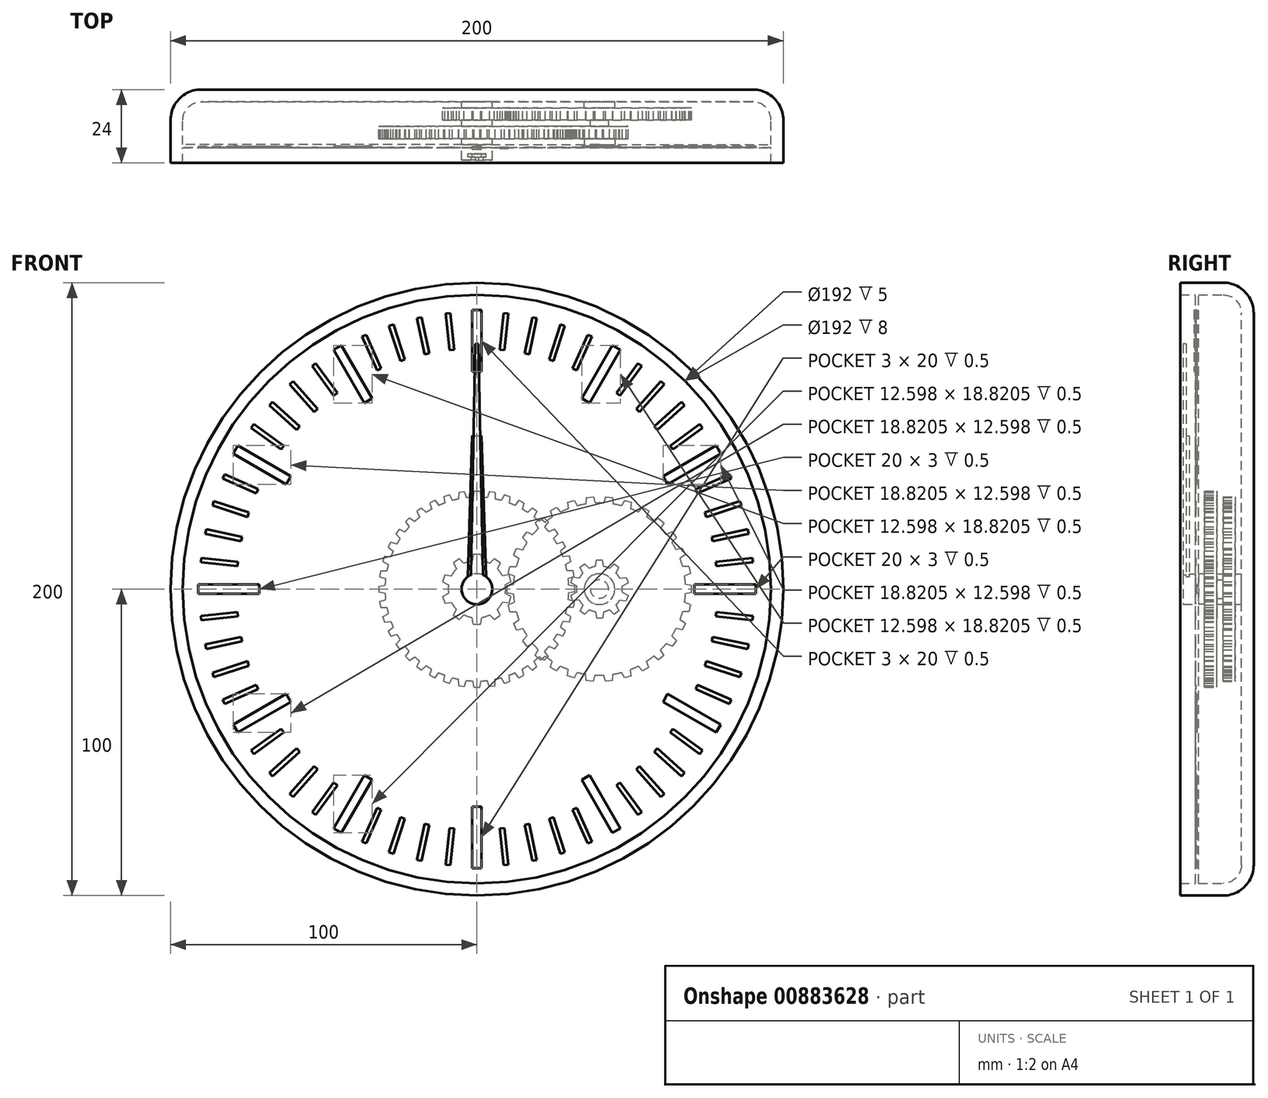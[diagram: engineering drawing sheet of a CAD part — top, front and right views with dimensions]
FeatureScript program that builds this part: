
annotation { "Feature Type Name" : "Feature", "Feature Type Description" : "" }
export const myFeature = defineFeature(function(context is Context, id is Id, definition is map)
    precondition{}
    {
        {
            var Q0;
            Q0=qCreatedBy(makeId("Front.planeOp"),FACE);
            var sketch = newSketch(context, id + "F0", { "sketchPlane" : qUnion([Q0])});
            skCircle(sketch, "E0", {"center": v(0, 0) * mm, "radius": 100 * mm});
            skSolve(sketch);
        }
        {
            var Q0;
            Q0 = qSketchRegion(id + "F0", true);
            extrude(context, id + "F1", {"entities" : qUnion([Q0]), "depth" : 24 * mm, "offsetDistance" : 25 * mm});
        }
        {
            var Q0;
            Q0=makeQuery(id+"F1.opExtrude","CAP_EDGE",EDGE,{"disambiguationData":[OSD([sQuery(id+"F0.wireOp",EDGE,"E0")])],"isStart":true});
            fillet(context, id + "F2", {"entities" : qUnion([Q0]), "radius" : 10 * mm, "tangentPropagation" : true, "allowEdgeOverflow" : false});
        }
        {
            var Q0;
            Q0=makeQuery(id+"F1.opExtrude","CAP_FACE",FACE,{"disambiguationData":[OSD([sQuery(id+"F0.wireOp",EDGE,"E0")])],"isStart":false});
            shell(context, id + "F3", {"entities" : qUnion([Q0]), "thickness" : 4 * mm});
        }
        {
            var Q0;
            {var subQ0=sQuery(id+"F0.wireOp",EDGE,"E0");Q0=makeQuery(id+"F3.opShell","OFFSET_FACE",FACE,{"disambiguationData":[OSD([subQ0]),TDD([makeQuery(id+"F1.opExtrude","CAP_FACE",FACE,{"disambiguationData":[OSD([subQ0])],"isStart":true})])]});}
            var sketch = newSketch(context, id + "F4", { "sketchPlane" : qUnion([Q0])});
            skCircle(sketch, "E1", {"center": v(0, 0) * mm, "radius": 3 * mm});
            skCircle(sketch, "E2", {"center": v(0, 0) * mm, "radius": 5 * mm});
            skCircle(sketch, "E3", {"center": v(40, 0) * mm, "radius": 3 * mm});
            skCircle(sketch, "E4", {"center": v(40, 0) * mm, "radius": 5 * mm});
            skSolve(sketch);
        }
        {
            var Q0;
            Q0 = qSketchRegion(id + "F4", true);
            extrude(context, id + "F5", {"entities" : qUnion([Q0]), "operationType" : NewBodyOperationType.ADD, "depth" : 2 * mm, "offsetDistance" : 25 * mm});
        }
        {
            var Q0;
            {var subQ0=sQuery(id+"F0.wireOp",EDGE,"E0");Q0=makeQuery(id+"F5.boolean.opBoolean","SPLIT",FACE,{"disambiguationData":[TD([makeQuery(id+"F5.opExtrude","SWEPT_FACE",FACE,{"disambiguationData":[OSD([sQuery(id+"F4.wireOp",EDGE,"E1")])]})])],"derivedFrom":makeQuery(id+"F3.opShell","OFFSET_FACE",FACE,{"disambiguationData":[OSD([subQ0]),TDD([makeQuery(id+"F1.opExtrude","CAP_FACE",FACE,{"disambiguationData":[OSD([subQ0])],"isStart":true})])]})});}
            extrude(context, id + "F6", {"entities" : qUnion([Q0]), "depth" : 19 * mm, "offsetDistance" : 25 * mm});
        }
        {
            var Q0;
            {var subQ0=sQuery(id+"F0.wireOp",EDGE,"E0");Q0=makeQuery(id+"F5.boolean.opBoolean","SPLIT",FACE,{"disambiguationData":[TD([makeQuery(id+"F5.opExtrude","SWEPT_FACE",FACE,{"disambiguationData":[OSD([sQuery(id+"F4.wireOp",EDGE,"E3")])]})])],"derivedFrom":makeQuery(id+"F3.opShell","OFFSET_FACE",FACE,{"disambiguationData":[OSD([subQ0]),TDD([makeQuery(id+"F1.opExtrude","CAP_FACE",FACE,{"disambiguationData":[OSD([subQ0])],"isStart":true})])]})});}
            extrude(context, id + "F7", {"entities" : qUnion([Q0]), "depth" : 8 * mm, "offsetDistance" : 25 * mm});
        }
        {
            var Q0;
            Q0=makeQuery(id+"F5.opExtrude","CAP_FACE",FACE,{"disambiguationData":[OSD([sQuery(id+"F4.wireOp",EDGE,"E1"),sQuery(id+"F4.wireOp",EDGE,"E2")])],"isStart":false});
            var sketch = newSketch(context, id + "F8", { "sketchPlane" : qUnion([Q0])});
            skCircle(sketch, "E5", {"center": v(0, 0) * mm, "radius": 9.38 * mm});
            skLineSegment(sketch, "E6", {"start": v(0, 11.38) * mm, "end": v(1.18, 11.38) * mm});
            skLineSegment(sketch, "E7", {"start": v(1.18, 11.38) * mm, "end": v(1.55, 9.25) * mm});
            skLineSegment(sketch, "E8.MirrorCS", {"start": v(0, 11.38) * mm, "end": v(-1.18, 11.38) * mm});
            skLineSegment(sketch, "E9.MirrorCS", {"start": v(-1.18, 11.38) * mm, "end": v(-1.55, 9.25) * mm});
            skLineSegment(sketch, "E10.1.0", {"start": v(-7.64, 8.51) * mm, "end": v(-6.7, 6.57) * mm});
            skLineSegment(sketch, "E10.1.1", {"start": v(-6.69, 9.2) * mm, "end": v(-7.64, 8.51) * mm});
            skLineSegment(sketch, "E10.1.2", {"start": v(-6.69, 9.2) * mm, "end": v(-5.73, 9.9) * mm});
            skLineSegment(sketch, "E10.1.3", {"start": v(-5.73, 9.9) * mm, "end": v(-4.18, 8.4) * mm});
            skLineSegment(sketch, "E10.2.0", {"start": v(-11.18, 2.4) * mm, "end": v(-9.27, 1.38) * mm});
            skLineSegment(sketch, "E10.2.1", {"start": v(-10.82, 3.52) * mm, "end": v(-11.18, 2.4) * mm});
            skLineSegment(sketch, "E10.2.2", {"start": v(-10.82, 3.52) * mm, "end": v(-10.45, 4.64) * mm});
            skLineSegment(sketch, "E10.2.3", {"start": v(-10.45, 4.64) * mm, "end": v(-8.31, 4.33) * mm});
            skLineSegment(sketch, "E11.2.3.0", {"start": v(-10.45, -4.64) * mm, "end": v(-8.31, -4.33) * mm});
            skLineSegment(sketch, "E11.3.3.0", {"start": v(-10.82, -3.52) * mm, "end": v(-10.45, -4.64) * mm});
            skLineSegment(sketch, "E11.6.3.0", {"start": v(-10.82, -3.52) * mm, "end": v(-11.18, -2.4) * mm});
            skLineSegment(sketch, "E11.9.3.0", {"start": v(-11.18, -2.4) * mm, "end": v(-9.27, -1.38) * mm});
            skLineSegment(sketch, "E11.2.4.0", {"start": v(-5.73, -9.9) * mm, "end": v(-4.18, -8.4) * mm});
            skLineSegment(sketch, "E11.3.4.0", {"start": v(-6.69, -9.2) * mm, "end": v(-5.73, -9.9) * mm});
            skLineSegment(sketch, "E11.6.4.0", {"start": v(-6.69, -9.2) * mm, "end": v(-7.64, -8.51) * mm});
            skLineSegment(sketch, "E11.9.4.0", {"start": v(-7.64, -8.51) * mm, "end": v(-6.7, -6.57) * mm});
            skLineSegment(sketch, "E11.2.5.0", {"start": v(1.18, -11.38) * mm, "end": v(1.55, -9.25) * mm});
            skLineSegment(sketch, "E11.3.5.0", {"start": v(0, -11.38) * mm, "end": v(1.18, -11.38) * mm});
            skLineSegment(sketch, "E11.6.5.0", {"start": v(0, -11.38) * mm, "end": v(-1.18, -11.38) * mm});
            skLineSegment(sketch, "E11.9.5.0", {"start": v(-1.18, -11.38) * mm, "end": v(-1.55, -9.25) * mm});
            skLineSegment(sketch, "E11.2.6.0", {"start": v(7.64, -8.51) * mm, "end": v(6.7, -6.57) * mm});
            skLineSegment(sketch, "E11.3.6.0", {"start": v(6.69, -9.2) * mm, "end": v(7.64, -8.51) * mm});
            skLineSegment(sketch, "E11.6.6.0", {"start": v(6.69, -9.2) * mm, "end": v(5.73, -9.9) * mm});
            skLineSegment(sketch, "E11.9.6.0", {"start": v(5.73, -9.9) * mm, "end": v(4.18, -8.4) * mm});
            skLineSegment(sketch, "E11.2.7.0", {"start": v(11.18, -2.4) * mm, "end": v(9.27, -1.38) * mm});
            skLineSegment(sketch, "E11.3.7.0", {"start": v(10.82, -3.52) * mm, "end": v(11.18, -2.4) * mm});
            skLineSegment(sketch, "E11.6.7.0", {"start": v(10.82, -3.52) * mm, "end": v(10.45, -4.64) * mm});
            skLineSegment(sketch, "E11.9.7.0", {"start": v(10.45, -4.64) * mm, "end": v(8.31, -4.33) * mm});
            skLineSegment(sketch, "E11.2.8.0", {"start": v(10.45, 4.64) * mm, "end": v(8.31, 4.33) * mm});
            skLineSegment(sketch, "E11.3.8.0", {"start": v(10.82, 3.52) * mm, "end": v(10.45, 4.64) * mm});
            skLineSegment(sketch, "E11.6.8.0", {"start": v(10.82, 3.52) * mm, "end": v(11.18, 2.4) * mm});
            skLineSegment(sketch, "E11.9.8.0", {"start": v(11.18, 2.4) * mm, "end": v(9.27, 1.38) * mm});
            skLineSegment(sketch, "E11.2.9.0", {"start": v(5.73, 9.9) * mm, "end": v(4.18, 8.4) * mm});
            skLineSegment(sketch, "E11.3.9.0", {"start": v(6.69, 9.2) * mm, "end": v(5.73, 9.9) * mm});
            skLineSegment(sketch, "E11.6.9.0", {"start": v(6.69, 9.2) * mm, "end": v(7.64, 8.51) * mm});
            skLineSegment(sketch, "E11.9.9.0", {"start": v(7.64, 8.51) * mm, "end": v(6.7, 6.57) * mm});
            skSolve(sketch);
        }
        {
            var Q0;
            Q0 = qSketchRegion(id + "F8", true);
            extrude(context, id + "F9", {"entities" : qUnion([Q0]), "operationType" : NewBodyOperationType.ADD, "depth" : 4 * mm, "offsetDistance" : 25 * mm});
        }
        {
            var Q0;
            Q0=makeQuery(id+"F5.opExtrude","CAP_FACE",FACE,{"disambiguationData":[OSD([sQuery(id+"F4.wireOp",EDGE,"E3"),sQuery(id+"F4.wireOp",EDGE,"E4")])],"isStart":false});
            var sketch = newSketch(context, id + "F10", { "sketchPlane" : qUnion([Q0])});
            skCircle(sketch, "E12", {"center": v(40, 0) * mm, "radius": 28.12 * mm});
            skLineSegment(sketch, "E13", {"start": v(9.88, 0) * mm, "end": v(9.88, 1.18) * mm});
            skLineSegment(sketch, "E14", {"start": v(9.88, 1.18) * mm, "end": v(11.92, 1.54) * mm});
            skLineSegment(sketch, "E15.MirrorCS", {"start": v(9.88, 0) * mm, "end": v(9.88, -1.18) * mm});
            skLineSegment(sketch, "E16.MirrorCS", {"start": v(9.88, -1.18) * mm, "end": v(11.92, -1.54) * mm});
            skLineSegment(sketch, "E17.1.0", {"start": v(10.29, -5.11) * mm, "end": v(12.21, -4.33) * mm});
            skLineSegment(sketch, "E17.1.1", {"start": v(10.53, -6.26) * mm, "end": v(10.29, -5.11) * mm});
            skLineSegment(sketch, "E17.1.2", {"start": v(10.53, -6.26) * mm, "end": v(10.78, -7.42) * mm});
            skLineSegment(sketch, "E17.1.3", {"start": v(10.78, -7.42) * mm, "end": v(12.85, -7.34) * mm});
            skLineSegment(sketch, "E17.2.0", {"start": v(12, -11.18) * mm, "end": v(13.72, -10.02) * mm});
            skLineSegment(sketch, "E17.2.1", {"start": v(12.48, -12.25) * mm, "end": v(12, -11.18) * mm});
            skLineSegment(sketch, "E17.2.2", {"start": v(12.48, -12.25) * mm, "end": v(12.96, -13.33) * mm});
            skLineSegment(sketch, "E17.2.3", {"start": v(12.96, -13.33) * mm, "end": v(14.97, -12.83) * mm});
            skLineSegment(sketch, "E18.1.3.0", {"start": v(14.94, -16.75) * mm, "end": v(16.38, -15.26) * mm});
            skLineSegment(sketch, "E18.3.3.0", {"start": v(15.63, -17.7) * mm, "end": v(14.94, -16.75) * mm});
            skLineSegment(sketch, "E18.6.3.0", {"start": v(15.63, -17.7) * mm, "end": v(16.32, -18.66) * mm});
            skLineSegment(sketch, "E18.9.3.0", {"start": v(16.32, -18.66) * mm, "end": v(18.18, -17.75) * mm});
            skLineSegment(sketch, "E18.1.4.0", {"start": v(18.97, -21.6) * mm, "end": v(20.07, -19.84) * mm});
            skLineSegment(sketch, "E18.3.4.0", {"start": v(19.84, -22.39) * mm, "end": v(18.97, -21.6) * mm});
            skLineSegment(sketch, "E18.6.4.0", {"start": v(19.84, -22.39) * mm, "end": v(20.72, -23.18) * mm});
            skLineSegment(sketch, "E18.9.4.0", {"start": v(20.72, -23.18) * mm, "end": v(22.35, -21.9) * mm});
            skLineSegment(sketch, "E18.1.5.0", {"start": v(23.92, -25.5) * mm, "end": v(24.63, -23.55) * mm});
            skLineSegment(sketch, "E18.3.5.0", {"start": v(24.94, -26.09) * mm, "end": v(23.92, -25.5) * mm});
            skLineSegment(sketch, "E18.6.5.0", {"start": v(24.94, -26.09) * mm, "end": v(25.96, -26.68) * mm});
            skLineSegment(sketch, "E18.9.5.0", {"start": v(25.96, -26.68) * mm, "end": v(27.3, -25.09) * mm});
            skLineSegment(sketch, "E18.1.6.0", {"start": v(29.57, -28.29) * mm, "end": v(29.86, -26.23) * mm});
            skLineSegment(sketch, "E18.3.6.0", {"start": v(30.7, -28.65) * mm, "end": v(29.57, -28.29) * mm});
            skLineSegment(sketch, "E18.6.6.0", {"start": v(30.7, -28.65) * mm, "end": v(31.81, -29.01) * mm});
            skLineSegment(sketch, "E18.9.6.0", {"start": v(31.81, -29.01) * mm, "end": v(32.78, -27.18) * mm});
            skLineSegment(sketch, "E18.1.7.0", {"start": v(35.68, -29.84) * mm, "end": v(35.53, -27.77) * mm});
            skLineSegment(sketch, "E18.3.7.0", {"start": v(36.85, -29.96) * mm, "end": v(35.68, -29.84) * mm});
            skLineSegment(sketch, "E18.6.7.0", {"start": v(36.85, -29.96) * mm, "end": v(38.02, -30.08) * mm});
            skLineSegment(sketch, "E18.9.7.0", {"start": v(38.02, -30.08) * mm, "end": v(38.6, -28.09) * mm});
            skLineSegment(sketch, "E18.1.8.0", {"start": v(41.98, -30.08) * mm, "end": v(41.4, -28.09) * mm});
            skLineSegment(sketch, "E18.3.8.0", {"start": v(43.15, -29.96) * mm, "end": v(41.98, -30.08) * mm});
            skLineSegment(sketch, "E18.6.8.0", {"start": v(43.15, -29.96) * mm, "end": v(44.32, -29.84) * mm});
            skLineSegment(sketch, "E18.9.8.0", {"start": v(44.32, -29.84) * mm, "end": v(44.47, -27.77) * mm});
            skLineSegment(sketch, "E18.1.9.0", {"start": v(48.19, -29.01) * mm, "end": v(47.22, -27.18) * mm});
            skLineSegment(sketch, "E18.3.9.0", {"start": v(49.3, -28.65) * mm, "end": v(48.19, -29.01) * mm});
            skLineSegment(sketch, "E18.6.9.0", {"start": v(49.3, -28.65) * mm, "end": v(50.43, -28.29) * mm});
            skLineSegment(sketch, "E18.9.9.0", {"start": v(50.43, -28.29) * mm, "end": v(50.14, -26.23) * mm});
            skLineSegment(sketch, "E18.1.10.0", {"start": v(54.04, -26.68) * mm, "end": v(52.7, -25.09) * mm});
            skLineSegment(sketch, "E18.3.10.0", {"start": v(55.06, -26.09) * mm, "end": v(54.04, -26.68) * mm});
            skLineSegment(sketch, "E18.6.10.0", {"start": v(55.06, -26.09) * mm, "end": v(56.08, -25.5) * mm});
            skLineSegment(sketch, "E18.9.10.0", {"start": v(56.08, -25.5) * mm, "end": v(55.37, -23.55) * mm});
            skLineSegment(sketch, "E18.1.11.0", {"start": v(59.28, -23.18) * mm, "end": v(57.65, -21.9) * mm});
            skLineSegment(sketch, "E18.3.11.0", {"start": v(60.16, -22.39) * mm, "end": v(59.28, -23.18) * mm});
            skLineSegment(sketch, "E18.6.11.0", {"start": v(60.16, -22.39) * mm, "end": v(61.03, -21.6) * mm});
            skLineSegment(sketch, "E18.9.11.0", {"start": v(61.03, -21.6) * mm, "end": v(59.93, -19.84) * mm});
            skLineSegment(sketch, "E18.1.12.0", {"start": v(63.68, -18.66) * mm, "end": v(61.82, -17.75) * mm});
            skLineSegment(sketch, "E18.3.12.0", {"start": v(64.37, -17.7) * mm, "end": v(63.68, -18.66) * mm});
            skLineSegment(sketch, "E18.6.12.0", {"start": v(64.37, -17.7) * mm, "end": v(65.06, -16.75) * mm});
            skLineSegment(sketch, "E18.9.12.0", {"start": v(65.06, -16.75) * mm, "end": v(63.62, -15.26) * mm});
            skLineSegment(sketch, "E18.1.13.0", {"start": v(67.04, -13.33) * mm, "end": v(65.03, -12.83) * mm});
            skLineSegment(sketch, "E18.3.13.0", {"start": v(67.52, -12.25) * mm, "end": v(67.04, -13.33) * mm});
            skLineSegment(sketch, "E18.6.13.0", {"start": v(67.52, -12.25) * mm, "end": v(68, -11.18) * mm});
            skLineSegment(sketch, "E18.9.13.0", {"start": v(68, -11.18) * mm, "end": v(66.28, -10.02) * mm});
            skLineSegment(sketch, "E18.1.14.0", {"start": v(69.22, -7.42) * mm, "end": v(67.15, -7.34) * mm});
            skLineSegment(sketch, "E18.3.14.0", {"start": v(69.47, -6.26) * mm, "end": v(69.22, -7.42) * mm});
            skLineSegment(sketch, "E18.6.14.0", {"start": v(69.47, -6.26) * mm, "end": v(69.71, -5.11) * mm});
            skLineSegment(sketch, "E18.9.14.0", {"start": v(69.71, -5.11) * mm, "end": v(67.79, -4.33) * mm});
            skLineSegment(sketch, "E18.1.15.0", {"start": v(70.12, -1.18) * mm, "end": v(68.08, -1.54) * mm});
            skLineSegment(sketch, "E18.3.15.0", {"start": v(70.12, 0) * mm, "end": v(70.12, -1.18) * mm});
            skLineSegment(sketch, "E18.6.15.0", {"start": v(70.12, 0) * mm, "end": v(70.12, 1.18) * mm});
            skLineSegment(sketch, "E18.9.15.0", {"start": v(70.12, 1.18) * mm, "end": v(68.08, 1.54) * mm});
            skLineSegment(sketch, "E18.1.16.0", {"start": v(69.71, 5.11) * mm, "end": v(67.79, 4.33) * mm});
            skLineSegment(sketch, "E18.3.16.0", {"start": v(69.47, 6.26) * mm, "end": v(69.71, 5.11) * mm});
            skLineSegment(sketch, "E18.6.16.0", {"start": v(69.47, 6.26) * mm, "end": v(69.22, 7.42) * mm});
            skLineSegment(sketch, "E18.9.16.0", {"start": v(69.22, 7.42) * mm, "end": v(67.15, 7.34) * mm});
            skLineSegment(sketch, "E18.1.17.0", {"start": v(68, 11.18) * mm, "end": v(66.28, 10.02) * mm});
            skLineSegment(sketch, "E18.3.17.0", {"start": v(67.52, 12.25) * mm, "end": v(68, 11.18) * mm});
            skLineSegment(sketch, "E18.6.17.0", {"start": v(67.52, 12.25) * mm, "end": v(67.04, 13.33) * mm});
            skLineSegment(sketch, "E18.9.17.0", {"start": v(67.04, 13.33) * mm, "end": v(65.03, 12.83) * mm});
            skLineSegment(sketch, "E18.1.18.0", {"start": v(65.06, 16.75) * mm, "end": v(63.62, 15.26) * mm});
            skLineSegment(sketch, "E18.3.18.0", {"start": v(64.37, 17.7) * mm, "end": v(65.06, 16.75) * mm});
            skLineSegment(sketch, "E18.6.18.0", {"start": v(64.37, 17.7) * mm, "end": v(63.68, 18.66) * mm});
            skLineSegment(sketch, "E18.9.18.0", {"start": v(63.68, 18.66) * mm, "end": v(61.82, 17.75) * mm});
            skLineSegment(sketch, "E18.1.19.0", {"start": v(61.03, 21.6) * mm, "end": v(59.93, 19.84) * mm});
            skLineSegment(sketch, "E18.3.19.0", {"start": v(60.16, 22.39) * mm, "end": v(61.03, 21.6) * mm});
            skLineSegment(sketch, "E18.6.19.0", {"start": v(60.16, 22.39) * mm, "end": v(59.28, 23.18) * mm});
            skLineSegment(sketch, "E18.9.19.0", {"start": v(59.28, 23.18) * mm, "end": v(57.65, 21.9) * mm});
            skLineSegment(sketch, "E18.1.20.0", {"start": v(56.08, 25.5) * mm, "end": v(55.37, 23.55) * mm});
            skLineSegment(sketch, "E18.3.20.0", {"start": v(55.06, 26.09) * mm, "end": v(56.08, 25.5) * mm});
            skLineSegment(sketch, "E18.6.20.0", {"start": v(55.06, 26.09) * mm, "end": v(54.04, 26.68) * mm});
            skLineSegment(sketch, "E18.9.20.0", {"start": v(54.04, 26.68) * mm, "end": v(52.7, 25.09) * mm});
            skLineSegment(sketch, "E18.1.21.0", {"start": v(50.43, 28.29) * mm, "end": v(50.14, 26.23) * mm});
            skLineSegment(sketch, "E18.3.21.0", {"start": v(49.3, 28.65) * mm, "end": v(50.43, 28.29) * mm});
            skLineSegment(sketch, "E18.6.21.0", {"start": v(49.3, 28.65) * mm, "end": v(48.19, 29.01) * mm});
            skLineSegment(sketch, "E18.9.21.0", {"start": v(48.19, 29.01) * mm, "end": v(47.22, 27.18) * mm});
            skLineSegment(sketch, "E18.1.22.0", {"start": v(44.32, 29.84) * mm, "end": v(44.47, 27.77) * mm});
            skLineSegment(sketch, "E18.3.22.0", {"start": v(43.15, 29.96) * mm, "end": v(44.32, 29.84) * mm});
            skLineSegment(sketch, "E18.6.22.0", {"start": v(43.15, 29.96) * mm, "end": v(41.98, 30.08) * mm});
            skLineSegment(sketch, "E18.9.22.0", {"start": v(41.98, 30.08) * mm, "end": v(41.4, 28.09) * mm});
            skLineSegment(sketch, "E18.1.23.0", {"start": v(38.02, 30.08) * mm, "end": v(38.6, 28.09) * mm});
            skLineSegment(sketch, "E18.3.23.0", {"start": v(36.85, 29.96) * mm, "end": v(38.02, 30.08) * mm});
            skLineSegment(sketch, "E18.6.23.0", {"start": v(36.85, 29.96) * mm, "end": v(35.68, 29.84) * mm});
            skLineSegment(sketch, "E18.9.23.0", {"start": v(35.68, 29.84) * mm, "end": v(35.53, 27.77) * mm});
            skLineSegment(sketch, "E18.1.24.0", {"start": v(31.81, 29.01) * mm, "end": v(32.78, 27.18) * mm});
            skLineSegment(sketch, "E18.3.24.0", {"start": v(30.7, 28.65) * mm, "end": v(31.81, 29.01) * mm});
            skLineSegment(sketch, "E18.6.24.0", {"start": v(30.7, 28.65) * mm, "end": v(29.57, 28.29) * mm});
            skLineSegment(sketch, "E18.9.24.0", {"start": v(29.57, 28.29) * mm, "end": v(29.86, 26.23) * mm});
            skLineSegment(sketch, "E18.1.25.0", {"start": v(25.96, 26.68) * mm, "end": v(27.3, 25.09) * mm});
            skLineSegment(sketch, "E18.3.25.0", {"start": v(24.94, 26.09) * mm, "end": v(25.96, 26.68) * mm});
            skLineSegment(sketch, "E18.6.25.0", {"start": v(24.94, 26.09) * mm, "end": v(23.92, 25.5) * mm});
            skLineSegment(sketch, "E18.9.25.0", {"start": v(23.92, 25.5) * mm, "end": v(24.63, 23.55) * mm});
            skLineSegment(sketch, "E18.1.26.0", {"start": v(20.72, 23.18) * mm, "end": v(22.35, 21.9) * mm});
            skLineSegment(sketch, "E18.3.26.0", {"start": v(19.84, 22.39) * mm, "end": v(20.72, 23.18) * mm});
            skLineSegment(sketch, "E18.6.26.0", {"start": v(19.84, 22.39) * mm, "end": v(18.97, 21.6) * mm});
            skLineSegment(sketch, "E18.9.26.0", {"start": v(18.97, 21.6) * mm, "end": v(20.07, 19.84) * mm});
            skLineSegment(sketch, "E18.1.27.0", {"start": v(16.32, 18.66) * mm, "end": v(18.18, 17.75) * mm});
            skLineSegment(sketch, "E18.3.27.0", {"start": v(15.63, 17.7) * mm, "end": v(16.32, 18.66) * mm});
            skLineSegment(sketch, "E18.6.27.0", {"start": v(15.63, 17.7) * mm, "end": v(14.94, 16.75) * mm});
            skLineSegment(sketch, "E18.9.27.0", {"start": v(14.94, 16.75) * mm, "end": v(16.38, 15.26) * mm});
            skLineSegment(sketch, "E18.1.28.0", {"start": v(12.96, 13.33) * mm, "end": v(14.97, 12.83) * mm});
            skLineSegment(sketch, "E18.3.28.0", {"start": v(12.48, 12.25) * mm, "end": v(12.96, 13.33) * mm});
            skLineSegment(sketch, "E18.6.28.0", {"start": v(12.48, 12.25) * mm, "end": v(12, 11.18) * mm});
            skLineSegment(sketch, "E18.9.28.0", {"start": v(12, 11.18) * mm, "end": v(13.72, 10.02) * mm});
            skLineSegment(sketch, "E18.1.29.0", {"start": v(10.78, 7.42) * mm, "end": v(12.85, 7.34) * mm});
            skLineSegment(sketch, "E18.3.29.0", {"start": v(10.53, 6.26) * mm, "end": v(10.78, 7.42) * mm});
            skLineSegment(sketch, "E18.6.29.0", {"start": v(10.53, 6.26) * mm, "end": v(10.29, 5.11) * mm});
            skLineSegment(sketch, "E18.9.29.0", {"start": v(10.29, 5.11) * mm, "end": v(12.21, 4.33) * mm});
            skSolve(sketch);
        }
        {
            var Q0;
            Q0 = qSketchRegion(id + "F10", true);
            extrude(context, id + "F11", {"entities" : qUnion([Q0]), "operationType" : NewBodyOperationType.ADD, "depth" : 4 * mm, "offsetDistance" : 25 * mm});
        }
        {
            var Q0;
            Q0=makeQuery(id+"F9.opExtrude","CAP_FACE",FACE,{"disambiguationData":[OSD([sQuery(id+"F8.wireOp",EDGE,"E5"),sQuery(id+"F8.wireOp",EDGE,"E6"),sQuery(id+"F8.wireOp",EDGE,"E7"),sQuery(id+"F8.wireOp",EDGE,"E8.MirrorCS"),sQuery(id+"F8.wireOp",EDGE,"E9.MirrorCS"),sQuery(id+"F8.wireOp",EDGE,"E10.1.0"),sQuery(id+"F8.wireOp",EDGE,"E10.1.1"),sQuery(id+"F8.wireOp",EDGE,"E10.1.2"),sQuery(id+"F8.wireOp",EDGE,"E10.1.3"),sQuery(id+"F8.wireOp",EDGE,"E10.2.0"),sQuery(id+"F8.wireOp",EDGE,"E10.2.1"),sQuery(id+"F8.wireOp",EDGE,"E10.2.2"),sQuery(id+"F8.wireOp",EDGE,"E10.2.3"),sQuery(id+"F8.wireOp",EDGE,"E11.2.3.0"),sQuery(id+"F8.wireOp",EDGE,"E11.3.3.0"),sQuery(id+"F8.wireOp",EDGE,"E11.6.3.0"),sQuery(id+"F8.wireOp",EDGE,"E11.9.3.0"),sQuery(id+"F8.wireOp",EDGE,"E11.2.4.0"),sQuery(id+"F8.wireOp",EDGE,"E11.3.4.0"),sQuery(id+"F8.wireOp",EDGE,"E11.6.4.0"),sQuery(id+"F8.wireOp",EDGE,"E11.9.4.0"),sQuery(id+"F8.wireOp",EDGE,"E11.2.5.0"),sQuery(id+"F8.wireOp",EDGE,"E11.3.5.0"),sQuery(id+"F8.wireOp",EDGE,"E11.6.5.0"),sQuery(id+"F8.wireOp",EDGE,"E11.9.5.0"),sQuery(id+"F8.wireOp",EDGE,"E11.2.6.0"),sQuery(id+"F8.wireOp",EDGE,"E11.3.6.0"),sQuery(id+"F8.wireOp",EDGE,"E11.6.6.0"),sQuery(id+"F8.wireOp",EDGE,"E11.9.6.0"),sQuery(id+"F8.wireOp",EDGE,"E11.2.7.0"),sQuery(id+"F8.wireOp",EDGE,"E11.3.7.0"),sQuery(id+"F8.wireOp",EDGE,"E11.6.7.0"),sQuery(id+"F8.wireOp",EDGE,"E11.9.7.0"),sQuery(id+"F8.wireOp",EDGE,"E11.2.8.0"),sQuery(id+"F8.wireOp",EDGE,"E11.3.8.0"),sQuery(id+"F8.wireOp",EDGE,"E11.6.8.0"),sQuery(id+"F8.wireOp",EDGE,"E11.9.8.0"),sQuery(id+"F8.wireOp",EDGE,"E11.2.9.0"),sQuery(id+"F8.wireOp",EDGE,"E11.3.9.0"),sQuery(id+"F8.wireOp",EDGE,"E11.6.9.0"),sQuery(id+"F8.wireOp",EDGE,"E11.9.9.0")])],"isStart":false});
            var sketch = newSketch(context, id + "F12", { "sketchPlane" : qUnion([Q0])});
            skCircle(sketch, "E19.0", {"center": v(0, 0) * mm, "radius": 5 * mm});
            skCircle(sketch, "E20.0", {"center": v(0, 0) * mm, "radius": 3 * mm});
            skSolve(sketch);
        }
        {
            var Q0;
            Q0 = qSketchRegion(id + "F12", true);
            extrude(context, id + "F13", {"entities" : qUnion([Q0]), "depth" : 2 * mm, "offsetDistance" : 25 * mm});
        }
        {
            var Q0;
            Q0=makeQuery(id+"F13.opExtrude","CAP_FACE",FACE,{"disambiguationData":[OSD([sQuery(id+"F12.wireOp",EDGE,"E19.0"),sQuery(id+"F12.wireOp",EDGE,"E20.0")])],"isStart":false});
            var sketch = newSketch(context, id + "F14", { "sketchPlane" : qUnion([Q0])});
            skCircle(sketch, "E21.0", {"center": v(0, 0) * mm, "radius": 3 * mm});
            skCircle(sketch, "E22", {"center": v(0, 0) * mm, "radius": 30 * mm});
            skLineSegment(sketch, "E23", {"start": v(0, 32) * mm, "end": v(0.94, 32) * mm});
            skLineSegment(sketch, "E24", {"start": v(0.94, 32) * mm, "end": v(1.3, 29.97) * mm});
            skLineSegment(sketch, "E25.MirrorCS", {"start": v(0, 32) * mm, "end": v(-0.94, 32) * mm});
            skLineSegment(sketch, "E26.MirrorCS", {"start": v(-0.94, 32) * mm, "end": v(-1.3, 29.97) * mm});
            skLineSegment(sketch, "E27.1.0", {"start": v(-5.94, 31.46) * mm, "end": v(-5.97, 29.4) * mm});
            skLineSegment(sketch, "E27.1.1", {"start": v(-5, 31.6) * mm, "end": v(-5.94, 31.46) * mm});
            skLineSegment(sketch, "E27.1.2", {"start": v(-5, 31.6) * mm, "end": v(-4.08, 31.75) * mm});
            skLineSegment(sketch, "E27.1.3", {"start": v(-4.08, 31.75) * mm, "end": v(-3.4, 29.8) * mm});
            skLineSegment(sketch, "E27.2.0", {"start": v(-10.78, 30.14) * mm, "end": v(-10.5, 28.1) * mm});
            skLineSegment(sketch, "E27.2.1", {"start": v(-9.89, 30.43) * mm, "end": v(-10.78, 30.14) * mm});
            skLineSegment(sketch, "E27.2.2", {"start": v(-9.89, 30.43) * mm, "end": v(-9, 30.73) * mm});
            skLineSegment(sketch, "E27.2.3", {"start": v(-9, 30.73) * mm, "end": v(-8.03, 28.9) * mm});
            skLineSegment(sketch, "E28.2.3.0", {"start": v(-15.37, 28.08) * mm, "end": v(-14.77, 26.11) * mm});
            skLineSegment(sketch, "E28.3.3.0", {"start": v(-14.53, 28.51) * mm, "end": v(-15.37, 28.08) * mm});
            skLineSegment(sketch, "E28.6.3.0", {"start": v(-14.53, 28.51) * mm, "end": v(-13.69, 28.94) * mm});
            skLineSegment(sketch, "E28.9.3.0", {"start": v(-13.69, 28.94) * mm, "end": v(-12.45, 27.3) * mm});
            skLineSegment(sketch, "E28.2.4.0", {"start": v(-19.57, 25.33) * mm, "end": v(-18.67, 23.48) * mm});
            skLineSegment(sketch, "E28.3.4.0", {"start": v(-18.8, 25.89) * mm, "end": v(-19.57, 25.33) * mm});
            skLineSegment(sketch, "E28.6.4.0", {"start": v(-18.8, 25.89) * mm, "end": v(-18.05, 26.44) * mm});
            skLineSegment(sketch, "E28.9.4.0", {"start": v(-18.05, 26.44) * mm, "end": v(-16.57, 25.01) * mm});
            skLineSegment(sketch, "E28.2.5.0", {"start": v(-23.3, 21.96) * mm, "end": v(-22.11, 20.27) * mm});
            skLineSegment(sketch, "E28.3.5.0", {"start": v(-22.63, 22.63) * mm, "end": v(-23.3, 21.96) * mm});
            skLineSegment(sketch, "E28.6.5.0", {"start": v(-22.63, 22.63) * mm, "end": v(-21.96, 23.3) * mm});
            skLineSegment(sketch, "E28.9.5.0", {"start": v(-21.96, 23.3) * mm, "end": v(-20.27, 22.11) * mm});
            skLineSegment(sketch, "E28.2.6.0", {"start": v(-26.44, 18.05) * mm, "end": v(-25.01, 16.57) * mm});
            skLineSegment(sketch, "E28.3.6.0", {"start": v(-25.89, 18.8) * mm, "end": v(-26.44, 18.05) * mm});
            skLineSegment(sketch, "E28.6.6.0", {"start": v(-25.89, 18.8) * mm, "end": v(-25.33, 19.57) * mm});
            skLineSegment(sketch, "E28.9.6.0", {"start": v(-25.33, 19.57) * mm, "end": v(-23.48, 18.67) * mm});
            skLineSegment(sketch, "E28.2.7.0", {"start": v(-28.94, 13.69) * mm, "end": v(-27.3, 12.45) * mm});
            skLineSegment(sketch, "E28.3.7.0", {"start": v(-28.51, 14.53) * mm, "end": v(-28.94, 13.69) * mm});
            skLineSegment(sketch, "E28.6.7.0", {"start": v(-28.51, 14.53) * mm, "end": v(-28.08, 15.37) * mm});
            skLineSegment(sketch, "E28.9.7.0", {"start": v(-28.08, 15.37) * mm, "end": v(-26.11, 14.77) * mm});
            skLineSegment(sketch, "E28.2.8.0", {"start": v(-30.73, 9) * mm, "end": v(-28.9, 8.03) * mm});
            skLineSegment(sketch, "E28.3.8.0", {"start": v(-30.43, 9.89) * mm, "end": v(-30.73, 9) * mm});
            skLineSegment(sketch, "E28.6.8.0", {"start": v(-30.43, 9.89) * mm, "end": v(-30.14, 10.78) * mm});
            skLineSegment(sketch, "E28.9.8.0", {"start": v(-30.14, 10.78) * mm, "end": v(-28.1, 10.5) * mm});
            skLineSegment(sketch, "E28.2.9.0", {"start": v(-31.75, 4.08) * mm, "end": v(-29.8, 3.4) * mm});
            skLineSegment(sketch, "E28.3.9.0", {"start": v(-31.6, 5) * mm, "end": v(-31.75, 4.08) * mm});
            skLineSegment(sketch, "E28.6.9.0", {"start": v(-31.6, 5) * mm, "end": v(-31.46, 5.94) * mm});
            skLineSegment(sketch, "E28.9.9.0", {"start": v(-31.46, 5.94) * mm, "end": v(-29.4, 5.97) * mm});
            skLineSegment(sketch, "E28.2.10.0", {"start": v(-32, -0.94) * mm, "end": v(-29.97, -1.3) * mm});
            skLineSegment(sketch, "E28.3.10.0", {"start": v(-32, 0) * mm, "end": v(-32, -0.94) * mm});
            skLineSegment(sketch, "E28.6.10.0", {"start": v(-32, 0) * mm, "end": v(-32, 0.94) * mm});
            skLineSegment(sketch, "E28.9.10.0", {"start": v(-32, 0.94) * mm, "end": v(-29.97, 1.3) * mm});
            skLineSegment(sketch, "E28.2.11.0", {"start": v(-31.46, -5.94) * mm, "end": v(-29.4, -5.97) * mm});
            skLineSegment(sketch, "E28.3.11.0", {"start": v(-31.6, -5) * mm, "end": v(-31.46, -5.94) * mm});
            skLineSegment(sketch, "E28.6.11.0", {"start": v(-31.6, -5) * mm, "end": v(-31.75, -4.08) * mm});
            skLineSegment(sketch, "E28.9.11.0", {"start": v(-31.75, -4.08) * mm, "end": v(-29.8, -3.4) * mm});
            skLineSegment(sketch, "E28.2.12.0", {"start": v(-30.14, -10.78) * mm, "end": v(-28.1, -10.5) * mm});
            skLineSegment(sketch, "E28.3.12.0", {"start": v(-30.43, -9.89) * mm, "end": v(-30.14, -10.78) * mm});
            skLineSegment(sketch, "E28.6.12.0", {"start": v(-30.43, -9.89) * mm, "end": v(-30.73, -9) * mm});
            skLineSegment(sketch, "E28.9.12.0", {"start": v(-30.73, -9) * mm, "end": v(-28.9, -8.03) * mm});
            skLineSegment(sketch, "E28.2.13.0", {"start": v(-28.08, -15.37) * mm, "end": v(-26.11, -14.77) * mm});
            skLineSegment(sketch, "E28.3.13.0", {"start": v(-28.51, -14.53) * mm, "end": v(-28.08, -15.37) * mm});
            skLineSegment(sketch, "E28.6.13.0", {"start": v(-28.51, -14.53) * mm, "end": v(-28.94, -13.69) * mm});
            skLineSegment(sketch, "E28.9.13.0", {"start": v(-28.94, -13.69) * mm, "end": v(-27.3, -12.45) * mm});
            skLineSegment(sketch, "E28.2.14.0", {"start": v(-25.33, -19.57) * mm, "end": v(-23.48, -18.67) * mm});
            skLineSegment(sketch, "E28.3.14.0", {"start": v(-25.89, -18.8) * mm, "end": v(-25.33, -19.57) * mm});
            skLineSegment(sketch, "E28.6.14.0", {"start": v(-25.89, -18.8) * mm, "end": v(-26.44, -18.05) * mm});
            skLineSegment(sketch, "E28.9.14.0", {"start": v(-26.44, -18.05) * mm, "end": v(-25.01, -16.57) * mm});
            skLineSegment(sketch, "E28.2.15.0", {"start": v(-21.96, -23.3) * mm, "end": v(-20.27, -22.11) * mm});
            skLineSegment(sketch, "E28.3.15.0", {"start": v(-22.63, -22.63) * mm, "end": v(-21.96, -23.3) * mm});
            skLineSegment(sketch, "E28.6.15.0", {"start": v(-22.63, -22.63) * mm, "end": v(-23.3, -21.96) * mm});
            skLineSegment(sketch, "E28.9.15.0", {"start": v(-23.3, -21.96) * mm, "end": v(-22.11, -20.27) * mm});
            skLineSegment(sketch, "E28.2.16.0", {"start": v(-18.05, -26.44) * mm, "end": v(-16.57, -25.01) * mm});
            skLineSegment(sketch, "E28.3.16.0", {"start": v(-18.8, -25.89) * mm, "end": v(-18.05, -26.44) * mm});
            skLineSegment(sketch, "E28.6.16.0", {"start": v(-18.8, -25.89) * mm, "end": v(-19.57, -25.33) * mm});
            skLineSegment(sketch, "E28.9.16.0", {"start": v(-19.57, -25.33) * mm, "end": v(-18.67, -23.48) * mm});
            skLineSegment(sketch, "E28.2.17.0", {"start": v(-13.69, -28.94) * mm, "end": v(-12.45, -27.3) * mm});
            skLineSegment(sketch, "E28.3.17.0", {"start": v(-14.53, -28.51) * mm, "end": v(-13.69, -28.94) * mm});
            skLineSegment(sketch, "E28.6.17.0", {"start": v(-14.53, -28.51) * mm, "end": v(-15.37, -28.08) * mm});
            skLineSegment(sketch, "E28.9.17.0", {"start": v(-15.37, -28.08) * mm, "end": v(-14.77, -26.11) * mm});
            skLineSegment(sketch, "E28.2.18.0", {"start": v(-9, -30.73) * mm, "end": v(-8.03, -28.9) * mm});
            skLineSegment(sketch, "E28.3.18.0", {"start": v(-9.89, -30.43) * mm, "end": v(-9, -30.73) * mm});
            skLineSegment(sketch, "E28.6.18.0", {"start": v(-9.89, -30.43) * mm, "end": v(-10.78, -30.14) * mm});
            skLineSegment(sketch, "E28.9.18.0", {"start": v(-10.78, -30.14) * mm, "end": v(-10.5, -28.1) * mm});
            skLineSegment(sketch, "E28.2.19.0", {"start": v(-4.08, -31.75) * mm, "end": v(-3.4, -29.8) * mm});
            skLineSegment(sketch, "E28.3.19.0", {"start": v(-5, -31.6) * mm, "end": v(-4.08, -31.75) * mm});
            skLineSegment(sketch, "E28.6.19.0", {"start": v(-5, -31.6) * mm, "end": v(-5.94, -31.46) * mm});
            skLineSegment(sketch, "E28.9.19.0", {"start": v(-5.94, -31.46) * mm, "end": v(-5.97, -29.4) * mm});
            skLineSegment(sketch, "E28.2.20.0", {"start": v(0.94, -32) * mm, "end": v(1.3, -29.97) * mm});
            skLineSegment(sketch, "E28.3.20.0", {"start": v(0, -32) * mm, "end": v(0.94, -32) * mm});
            skLineSegment(sketch, "E28.6.20.0", {"start": v(0, -32) * mm, "end": v(-0.94, -32) * mm});
            skLineSegment(sketch, "E28.9.20.0", {"start": v(-0.94, -32) * mm, "end": v(-1.3, -29.97) * mm});
            skLineSegment(sketch, "E28.2.21.0", {"start": v(5.94, -31.46) * mm, "end": v(5.97, -29.4) * mm});
            skLineSegment(sketch, "E28.3.21.0", {"start": v(5, -31.6) * mm, "end": v(5.94, -31.46) * mm});
            skLineSegment(sketch, "E28.6.21.0", {"start": v(5, -31.6) * mm, "end": v(4.08, -31.75) * mm});
            skLineSegment(sketch, "E28.9.21.0", {"start": v(4.08, -31.75) * mm, "end": v(3.4, -29.8) * mm});
            skLineSegment(sketch, "E28.2.22.0", {"start": v(10.78, -30.14) * mm, "end": v(10.5, -28.1) * mm});
            skLineSegment(sketch, "E28.3.22.0", {"start": v(9.89, -30.43) * mm, "end": v(10.78, -30.14) * mm});
            skLineSegment(sketch, "E28.6.22.0", {"start": v(9.89, -30.43) * mm, "end": v(9, -30.73) * mm});
            skLineSegment(sketch, "E28.9.22.0", {"start": v(9, -30.73) * mm, "end": v(8.03, -28.9) * mm});
            skLineSegment(sketch, "E28.2.23.0", {"start": v(15.37, -28.08) * mm, "end": v(14.77, -26.11) * mm});
            skLineSegment(sketch, "E28.3.23.0", {"start": v(14.53, -28.51) * mm, "end": v(15.37, -28.08) * mm});
            skLineSegment(sketch, "E28.6.23.0", {"start": v(14.53, -28.51) * mm, "end": v(13.69, -28.94) * mm});
            skLineSegment(sketch, "E28.9.23.0", {"start": v(13.69, -28.94) * mm, "end": v(12.45, -27.3) * mm});
            skLineSegment(sketch, "E28.2.24.0", {"start": v(19.57, -25.33) * mm, "end": v(18.67, -23.48) * mm});
            skLineSegment(sketch, "E28.3.24.0", {"start": v(18.8, -25.89) * mm, "end": v(19.57, -25.33) * mm});
            skLineSegment(sketch, "E28.6.24.0", {"start": v(18.8, -25.89) * mm, "end": v(18.05, -26.44) * mm});
            skLineSegment(sketch, "E28.9.24.0", {"start": v(18.05, -26.44) * mm, "end": v(16.57, -25.01) * mm});
            skLineSegment(sketch, "E28.2.25.0", {"start": v(23.3, -21.96) * mm, "end": v(22.11, -20.27) * mm});
            skLineSegment(sketch, "E28.3.25.0", {"start": v(22.63, -22.63) * mm, "end": v(23.3, -21.96) * mm});
            skLineSegment(sketch, "E28.6.25.0", {"start": v(22.63, -22.63) * mm, "end": v(21.96, -23.3) * mm});
            skLineSegment(sketch, "E28.9.25.0", {"start": v(21.96, -23.3) * mm, "end": v(20.27, -22.11) * mm});
            skLineSegment(sketch, "E28.2.26.0", {"start": v(26.44, -18.05) * mm, "end": v(25.01, -16.57) * mm});
            skLineSegment(sketch, "E28.3.26.0", {"start": v(25.89, -18.8) * mm, "end": v(26.44, -18.05) * mm});
            skLineSegment(sketch, "E28.6.26.0", {"start": v(25.89, -18.8) * mm, "end": v(25.33, -19.57) * mm});
            skLineSegment(sketch, "E28.9.26.0", {"start": v(25.33, -19.57) * mm, "end": v(23.48, -18.67) * mm});
            skLineSegment(sketch, "E28.2.27.0", {"start": v(28.94, -13.69) * mm, "end": v(27.3, -12.45) * mm});
            skLineSegment(sketch, "E28.3.27.0", {"start": v(28.51, -14.53) * mm, "end": v(28.94, -13.69) * mm});
            skLineSegment(sketch, "E28.6.27.0", {"start": v(28.51, -14.53) * mm, "end": v(28.08, -15.37) * mm});
            skLineSegment(sketch, "E28.9.27.0", {"start": v(28.08, -15.37) * mm, "end": v(26.11, -14.77) * mm});
            skLineSegment(sketch, "E28.2.28.0", {"start": v(30.73, -9) * mm, "end": v(28.9, -8.03) * mm});
            skLineSegment(sketch, "E28.3.28.0", {"start": v(30.43, -9.89) * mm, "end": v(30.73, -9) * mm});
            skLineSegment(sketch, "E28.6.28.0", {"start": v(30.43, -9.89) * mm, "end": v(30.14, -10.78) * mm});
            skLineSegment(sketch, "E28.9.28.0", {"start": v(30.14, -10.78) * mm, "end": v(28.1, -10.5) * mm});
            skLineSegment(sketch, "E28.2.29.0", {"start": v(31.75, -4.08) * mm, "end": v(29.8, -3.4) * mm});
            skLineSegment(sketch, "E28.3.29.0", {"start": v(31.6, -5) * mm, "end": v(31.75, -4.08) * mm});
            skLineSegment(sketch, "E28.6.29.0", {"start": v(31.6, -5) * mm, "end": v(31.46, -5.94) * mm});
            skLineSegment(sketch, "E28.9.29.0", {"start": v(31.46, -5.94) * mm, "end": v(29.4, -5.97) * mm});
            skLineSegment(sketch, "E28.2.30.0", {"start": v(32, 0.94) * mm, "end": v(29.97, 1.3) * mm});
            skLineSegment(sketch, "E28.3.30.0", {"start": v(32, 0) * mm, "end": v(32, 0.94) * mm});
            skLineSegment(sketch, "E28.6.30.0", {"start": v(32, 0) * mm, "end": v(32, -0.94) * mm});
            skLineSegment(sketch, "E28.9.30.0", {"start": v(32, -0.94) * mm, "end": v(29.97, -1.3) * mm});
            skLineSegment(sketch, "E28.2.31.0", {"start": v(31.46, 5.94) * mm, "end": v(29.4, 5.97) * mm});
            skLineSegment(sketch, "E28.3.31.0", {"start": v(31.6, 5) * mm, "end": v(31.46, 5.94) * mm});
            skLineSegment(sketch, "E28.6.31.0", {"start": v(31.6, 5) * mm, "end": v(31.75, 4.08) * mm});
            skLineSegment(sketch, "E28.9.31.0", {"start": v(31.75, 4.08) * mm, "end": v(29.8, 3.4) * mm});
            skLineSegment(sketch, "E28.2.32.0", {"start": v(30.14, 10.78) * mm, "end": v(28.1, 10.5) * mm});
            skLineSegment(sketch, "E28.3.32.0", {"start": v(30.43, 9.89) * mm, "end": v(30.14, 10.78) * mm});
            skLineSegment(sketch, "E28.6.32.0", {"start": v(30.43, 9.89) * mm, "end": v(30.73, 9) * mm});
            skLineSegment(sketch, "E28.9.32.0", {"start": v(30.73, 9) * mm, "end": v(28.9, 8.03) * mm});
            skLineSegment(sketch, "E28.2.33.0", {"start": v(28.08, 15.37) * mm, "end": v(26.11, 14.77) * mm});
            skLineSegment(sketch, "E28.3.33.0", {"start": v(28.51, 14.53) * mm, "end": v(28.08, 15.37) * mm});
            skLineSegment(sketch, "E28.6.33.0", {"start": v(28.51, 14.53) * mm, "end": v(28.94, 13.69) * mm});
            skLineSegment(sketch, "E28.9.33.0", {"start": v(28.94, 13.69) * mm, "end": v(27.3, 12.45) * mm});
            skLineSegment(sketch, "E28.2.34.0", {"start": v(25.33, 19.57) * mm, "end": v(23.48, 18.67) * mm});
            skLineSegment(sketch, "E28.3.34.0", {"start": v(25.89, 18.8) * mm, "end": v(25.33, 19.57) * mm});
            skLineSegment(sketch, "E28.6.34.0", {"start": v(25.89, 18.8) * mm, "end": v(26.44, 18.05) * mm});
            skLineSegment(sketch, "E28.9.34.0", {"start": v(26.44, 18.05) * mm, "end": v(25.01, 16.57) * mm});
            skLineSegment(sketch, "E28.2.35.0", {"start": v(21.96, 23.3) * mm, "end": v(20.27, 22.11) * mm});
            skLineSegment(sketch, "E28.3.35.0", {"start": v(22.63, 22.63) * mm, "end": v(21.96, 23.3) * mm});
            skLineSegment(sketch, "E28.6.35.0", {"start": v(22.63, 22.63) * mm, "end": v(23.3, 21.96) * mm});
            skLineSegment(sketch, "E28.9.35.0", {"start": v(23.3, 21.96) * mm, "end": v(22.11, 20.27) * mm});
            skLineSegment(sketch, "E28.2.36.0", {"start": v(18.05, 26.44) * mm, "end": v(16.57, 25.01) * mm});
            skLineSegment(sketch, "E28.3.36.0", {"start": v(18.8, 25.89) * mm, "end": v(18.05, 26.44) * mm});
            skLineSegment(sketch, "E28.6.36.0", {"start": v(18.8, 25.89) * mm, "end": v(19.57, 25.33) * mm});
            skLineSegment(sketch, "E28.9.36.0", {"start": v(19.57, 25.33) * mm, "end": v(18.67, 23.48) * mm});
            skLineSegment(sketch, "E28.2.37.0", {"start": v(13.69, 28.94) * mm, "end": v(12.45, 27.3) * mm});
            skLineSegment(sketch, "E28.3.37.0", {"start": v(14.53, 28.51) * mm, "end": v(13.69, 28.94) * mm});
            skLineSegment(sketch, "E28.6.37.0", {"start": v(14.53, 28.51) * mm, "end": v(15.37, 28.08) * mm});
            skLineSegment(sketch, "E28.9.37.0", {"start": v(15.37, 28.08) * mm, "end": v(14.77, 26.11) * mm});
            skLineSegment(sketch, "E28.2.38.0", {"start": v(9, 30.73) * mm, "end": v(8.03, 28.9) * mm});
            skLineSegment(sketch, "E28.3.38.0", {"start": v(9.89, 30.43) * mm, "end": v(9, 30.73) * mm});
            skLineSegment(sketch, "E28.6.38.0", {"start": v(9.89, 30.43) * mm, "end": v(10.78, 30.14) * mm});
            skLineSegment(sketch, "E28.9.38.0", {"start": v(10.78, 30.14) * mm, "end": v(10.5, 28.1) * mm});
            skLineSegment(sketch, "E28.2.39.0", {"start": v(4.08, 31.75) * mm, "end": v(3.4, 29.8) * mm});
            skLineSegment(sketch, "E28.3.39.0", {"start": v(5, 31.6) * mm, "end": v(4.08, 31.75) * mm});
            skLineSegment(sketch, "E28.6.39.0", {"start": v(5, 31.6) * mm, "end": v(5.94, 31.46) * mm});
            skLineSegment(sketch, "E28.9.39.0", {"start": v(5.94, 31.46) * mm, "end": v(5.97, 29.4) * mm});
            skSolve(sketch);
        }
        {
            var Q0;
            Q0 = qSketchRegion(id + "F14", true);
            extrude(context, id + "F15", {"entities" : qUnion([Q0]), "operationType" : NewBodyOperationType.ADD, "depth" : 4 * mm, "offsetDistance" : 25 * mm});
        }
        {
            var Q0;
            Q0=makeQuery(id+"F7.opExtrude","CAP_FACE",FACE,{"disambiguationData":[OSD([sQuery(id+"F0.wireOp",EDGE,"E0")])],"isStart":false});
            var sketch = newSketch(context, id + "F16", { "sketchPlane" : qUnion([Q0])});
            skCircle(sketch, "E29", {"center": v(40, 0) * mm, "radius": 7.5 * mm});
            skLineSegment(sketch, "E30", {"start": v(40, 0) * mm, "end": v(40, 7.5) * mm, "construction": true});
            skLineSegment(sketch, "E31", {"start": v(38.68, 7.38) * mm, "end": v(39.06, 9.5) * mm});
            skLineSegment(sketch, "E32", {"start": v(39.06, 9.5) * mm, "end": v(40.94, 9.5) * mm});
            skLineSegment(sketch, "E33.MirrorCS", {"start": v(41.32, 7.38) * mm, "end": v(40.94, 9.5) * mm});
            skLineSegment(sketch, "E34.1.0", {"start": v(34.6, 5.2) * mm, "end": v(33.65, 7.13) * mm});
            skLineSegment(sketch, "E34.1.1", {"start": v(33.65, 7.13) * mm, "end": v(35.18, 8.24) * mm});
            skLineSegment(sketch, "E34.1.2", {"start": v(36.72, 6.75) * mm, "end": v(35.18, 8.24) * mm});
            skLineSegment(sketch, "E34.2.0", {"start": v(32.57, 1.03) * mm, "end": v(30.67, 2.04) * mm});
            skLineSegment(sketch, "E34.2.1", {"start": v(30.67, 2.04) * mm, "end": v(31.26, 3.83) * mm});
            skLineSegment(sketch, "E34.2.2", {"start": v(33.38, 3.53) * mm, "end": v(31.26, 3.83) * mm});
            skLineSegment(sketch, "E35.1.3.0", {"start": v(33.38, -3.53) * mm, "end": v(31.26, -3.83) * mm});
            skLineSegment(sketch, "E35.3.3.0", {"start": v(31.26, -3.83) * mm, "end": v(30.67, -2.04) * mm});
            skLineSegment(sketch, "E35.6.3.0", {"start": v(32.57, -1.03) * mm, "end": v(30.67, -2.04) * mm});
            skLineSegment(sketch, "E35.1.4.0", {"start": v(36.72, -6.75) * mm, "end": v(35.18, -8.24) * mm});
            skLineSegment(sketch, "E35.3.4.0", {"start": v(35.18, -8.24) * mm, "end": v(33.65, -7.13) * mm});
            skLineSegment(sketch, "E35.6.4.0", {"start": v(34.6, -5.2) * mm, "end": v(33.65, -7.13) * mm});
            skLineSegment(sketch, "E35.1.5.0", {"start": v(41.32, -7.38) * mm, "end": v(40.94, -9.5) * mm});
            skLineSegment(sketch, "E35.3.5.0", {"start": v(40.94, -9.5) * mm, "end": v(39.06, -9.5) * mm});
            skLineSegment(sketch, "E35.6.5.0", {"start": v(38.68, -7.38) * mm, "end": v(39.06, -9.5) * mm});
            skLineSegment(sketch, "E35.1.6.0", {"start": v(45.4, -5.2) * mm, "end": v(46.35, -7.13) * mm});
            skLineSegment(sketch, "E35.3.6.0", {"start": v(46.35, -7.13) * mm, "end": v(44.82, -8.24) * mm});
            skLineSegment(sketch, "E35.6.6.0", {"start": v(43.28, -6.75) * mm, "end": v(44.82, -8.24) * mm});
            skLineSegment(sketch, "E35.1.7.0", {"start": v(47.43, -1.03) * mm, "end": v(49.33, -2.04) * mm});
            skLineSegment(sketch, "E35.3.7.0", {"start": v(49.33, -2.04) * mm, "end": v(48.74, -3.83) * mm});
            skLineSegment(sketch, "E35.6.7.0", {"start": v(46.62, -3.53) * mm, "end": v(48.74, -3.83) * mm});
            skLineSegment(sketch, "E35.1.8.0", {"start": v(46.62, 3.53) * mm, "end": v(48.74, 3.83) * mm});
            skLineSegment(sketch, "E35.3.8.0", {"start": v(48.74, 3.83) * mm, "end": v(49.33, 2.04) * mm});
            skLineSegment(sketch, "E35.6.8.0", {"start": v(47.43, 1.03) * mm, "end": v(49.33, 2.04) * mm});
            skLineSegment(sketch, "E35.1.9.0", {"start": v(43.28, 6.75) * mm, "end": v(44.82, 8.24) * mm});
            skLineSegment(sketch, "E35.3.9.0", {"start": v(44.82, 8.24) * mm, "end": v(46.35, 7.13) * mm});
            skLineSegment(sketch, "E35.6.9.0", {"start": v(45.4, 5.2) * mm, "end": v(46.35, 7.13) * mm});
            skSolve(sketch);
        }
        {
            var Q0;
            Q0 = qSketchRegion(id + "F16", true);
            extrude(context, id + "F17", {"entities" : qUnion([Q0]), "operationType" : NewBodyOperationType.ADD, "depth" : 4 * mm, "offsetDistance" : 25 * mm});
        }
        {
            var Q0;
            Q0=makeQuery(id+"F17.opExtrude","CAP_FACE",FACE,{"disambiguationData":[OSD([sQuery(id+"F16.wireOp",EDGE,"E29"),sQuery(id+"F16.wireOp",EDGE,"E31"),sQuery(id+"F16.wireOp",EDGE,"E32"),sQuery(id+"F16.wireOp",EDGE,"E33.MirrorCS"),sQuery(id+"F16.wireOp",EDGE,"E34.1.0"),sQuery(id+"F16.wireOp",EDGE,"E34.1.1"),sQuery(id+"F16.wireOp",EDGE,"E34.1.2"),sQuery(id+"F16.wireOp",EDGE,"E34.2.0"),sQuery(id+"F16.wireOp",EDGE,"E34.2.1"),sQuery(id+"F16.wireOp",EDGE,"E34.2.2"),sQuery(id+"F16.wireOp",EDGE,"E35.1.3.0"),sQuery(id+"F16.wireOp",EDGE,"E35.3.3.0"),sQuery(id+"F16.wireOp",EDGE,"E35.6.3.0"),sQuery(id+"F16.wireOp",EDGE,"E35.1.4.0"),sQuery(id+"F16.wireOp",EDGE,"E35.3.4.0"),sQuery(id+"F16.wireOp",EDGE,"E35.6.4.0"),sQuery(id+"F16.wireOp",EDGE,"E35.1.5.0"),sQuery(id+"F16.wireOp",EDGE,"E35.3.5.0"),sQuery(id+"F16.wireOp",EDGE,"E35.6.5.0"),sQuery(id+"F16.wireOp",EDGE,"E35.1.6.0"),sQuery(id+"F16.wireOp",EDGE,"E35.3.6.0"),sQuery(id+"F16.wireOp",EDGE,"E35.6.6.0"),sQuery(id+"F16.wireOp",EDGE,"E35.1.7.0"),sQuery(id+"F16.wireOp",EDGE,"E35.3.7.0"),sQuery(id+"F16.wireOp",EDGE,"E35.6.7.0"),sQuery(id+"F16.wireOp",EDGE,"E35.1.8.0"),sQuery(id+"F16.wireOp",EDGE,"E35.3.8.0"),sQuery(id+"F16.wireOp",EDGE,"E35.6.8.0"),sQuery(id+"F16.wireOp",EDGE,"E35.1.9.0"),sQuery(id+"F16.wireOp",EDGE,"E35.3.9.0"),sQuery(id+"F16.wireOp",EDGE,"E35.6.9.0")])],"isStart":false});
            var sketch = newSketch(context, id + "F18", { "sketchPlane" : qUnion([Q0])});
            skCircle(sketch, "E36.0", {"center": v(40, 0) * mm, "radius": 3 * mm});
            skSolve(sketch);
        }
        {
            var Q0;
            Q0 = qSketchRegion(id + "F18", true);
            extrude(context, id + "F19", {"entities" : qUnion([Q0]), "operationType" : NewBodyOperationType.ADD, "depth" : 2 * mm, "offsetDistance" : 25 * mm});
        }
        {
            var Q0;
            Q0=makeQuery(id+"F19.opExtrude","CAP_FACE",FACE,{"disambiguationData":[OSD([sQuery(id+"F18.wireOp",EDGE,"E36.0")])],"isStart":false});
            var sketch = newSketch(context, id + "F20", { "sketchPlane" : qUnion([Q0])});
            skCircle(sketch, "E37", {"center": v(0, 0) * mm, "radius": 98 * mm});
            skCircle(sketch, "E38.0", {"center": v(0, 0) * mm, "radius": 5 * mm});
            skSolve(sketch);
        }
        {
            var Q0;
            Q0 = qSketchRegion(id + "F20", true);
            extrude(context, id + "F21", {"entities" : qUnion([Q0]), "depth" : 1 * mm, "offsetDistance" : 25 * mm});
        }
        {
            var Q0;
            Q0=makeQuery(id+"F21.opExtrude","SWEPT_BODY",BODY,{"disambiguationData":[OSD([sQuery(id+"F20.wireOp",EDGE,"E37"),sQuery(id+"F20.wireOp",EDGE,"E38.0")])]});
            var Q1;
            Q1=makeQuery(id+"F1.opExtrude","SWEPT_BODY",BODY,{"disambiguationData":[OSD([sQuery(id+"F0.wireOp",EDGE,"E0")])]});
            booleanBodies(context, id + "F22", {"operationType" : BooleanOperationType.SUBTRACTION, "tools" : qUnion([Q0]), "targets" : qUnion([Q1]), "keepTools" : true});
        }
        {
            var Q0;
            Q0=makeQuery(id+"F21.opExtrude","CAP_FACE",FACE,{"disambiguationData":[OSD([sQuery(id+"F20.wireOp",EDGE,"E37"),sQuery(id+"F20.wireOp",EDGE,"E38.0")])],"isStart":true});
            var sketch = newSketch(context, id + "F23", { "sketchPlane" : qUnion([Q0])});
            skCircle(sketch, "E39.0", {"center": v(-40, 0) * mm, "radius": 3 * mm});
            skCircle(sketch, "E40", {"center": v(-40, 0) * mm, "radius": 5 * mm});
            skSolve(sketch);
        }
        {
            var Q0;
            Q0 = qSketchRegion(id + "F23", true);
            extrude(context, id + "F24", {"entities" : qUnion([Q0]), "operationType" : NewBodyOperationType.ADD, "endBound" : BoundingType.UP_TO_NEXT, "depth" : 25 * mm, "offsetDistance" : 25 * mm});
        }
        {
            var Q0;
            Q0=makeQuery(id+"F21.opExtrude","CAP_FACE",FACE,{"disambiguationData":[OSD([sQuery(id+"F20.wireOp",EDGE,"E37"),sQuery(id+"F20.wireOp",EDGE,"E38.0")])],"isStart":false});
            var sketch = newSketch(context, id + "F25", { "sketchPlane" : qUnion([Q0])});
            skLineSegment(sketch, "E41.bottom", {"start": v(-1.5, 91) * mm, "end": v(1.5, 91) * mm});
            skLineSegment(sketch, "E41.top", {"start": v(-1.5, 71) * mm, "end": v(1.5, 71) * mm});
            skLineSegment(sketch, "E41.left", {"start": v(-1.5, 91) * mm, "end": v(-1.5, 71) * mm});
            skLineSegment(sketch, "E41.right", {"start": v(1.5, 91) * mm, "end": v(1.5, 71) * mm});
            skPoint(sketch, "E41.middle", {"position": v(0, 81) * mm});
            skLineSegment(sketch, "E42.1.0", {"start": v(-46.8, 78.06) * mm, "end": v(-44.2, 79.56) * mm});
            skLineSegment(sketch, "E42.1.1", {"start": v(-46.8, 78.06) * mm, "end": v(-36.8, 60.74) * mm});
            skLineSegment(sketch, "E42.1.2", {"start": v(-44.2, 79.56) * mm, "end": v(-34.2, 62.24) * mm});
            skLineSegment(sketch, "E42.1.3", {"start": v(-36.8, 60.74) * mm, "end": v(-34.2, 62.24) * mm});
            skLineSegment(sketch, "E42.2.0", {"start": v(-79.56, 44.2) * mm, "end": v(-78.06, 46.8) * mm});
            skLineSegment(sketch, "E42.2.1", {"start": v(-79.56, 44.2) * mm, "end": v(-62.24, 34.2) * mm});
            skLineSegment(sketch, "E42.2.2", {"start": v(-78.06, 46.8) * mm, "end": v(-60.74, 36.8) * mm});
            skLineSegment(sketch, "E42.2.3", {"start": v(-62.24, 34.2) * mm, "end": v(-60.74, 36.8) * mm});
            skPoint(sketch, "E42.center", {"position": v(0, 0) * mm});
            skLineSegment(sketch, "E43.1.3.0", {"start": v(-91, -1.5) * mm, "end": v(-91, 1.5) * mm});
            skLineSegment(sketch, "E43.3.3.0", {"start": v(-91, -1.5) * mm, "end": v(-71, -1.5) * mm});
            skLineSegment(sketch, "E43.6.3.0", {"start": v(-91, 1.5) * mm, "end": v(-71, 1.5) * mm});
            skLineSegment(sketch, "E43.9.3.0", {"start": v(-71, -1.5) * mm, "end": v(-71, 1.5) * mm});
            skLineSegment(sketch, "E43.1.4.0", {"start": v(-78.06, -46.8) * mm, "end": v(-79.56, -44.2) * mm});
            skLineSegment(sketch, "E43.3.4.0", {"start": v(-78.06, -46.8) * mm, "end": v(-60.74, -36.8) * mm});
            skLineSegment(sketch, "E43.6.4.0", {"start": v(-79.56, -44.2) * mm, "end": v(-62.24, -34.2) * mm});
            skLineSegment(sketch, "E43.9.4.0", {"start": v(-60.74, -36.8) * mm, "end": v(-62.24, -34.2) * mm});
            skLineSegment(sketch, "E43.1.5.0", {"start": v(-44.2, -79.56) * mm, "end": v(-46.8, -78.06) * mm});
            skLineSegment(sketch, "E43.3.5.0", {"start": v(-44.2, -79.56) * mm, "end": v(-34.2, -62.24) * mm});
            skLineSegment(sketch, "E43.6.5.0", {"start": v(-46.8, -78.06) * mm, "end": v(-36.8, -60.74) * mm});
            skLineSegment(sketch, "E43.9.5.0", {"start": v(-34.2, -62.24) * mm, "end": v(-36.8, -60.74) * mm});
            skLineSegment(sketch, "E43.1.6.0", {"start": v(1.5, -91) * mm, "end": v(-1.5, -91) * mm});
            skLineSegment(sketch, "E43.3.6.0", {"start": v(1.5, -91) * mm, "end": v(1.5, -71) * mm});
            skLineSegment(sketch, "E43.6.6.0", {"start": v(-1.5, -91) * mm, "end": v(-1.5, -71) * mm});
            skLineSegment(sketch, "E43.9.6.0", {"start": v(1.5, -71) * mm, "end": v(-1.5, -71) * mm});
            skLineSegment(sketch, "E43.1.7.0", {"start": v(46.8, -78.06) * mm, "end": v(44.2, -79.56) * mm});
            skLineSegment(sketch, "E43.3.7.0", {"start": v(46.8, -78.06) * mm, "end": v(36.8, -60.74) * mm});
            skLineSegment(sketch, "E43.6.7.0", {"start": v(44.2, -79.56) * mm, "end": v(34.2, -62.24) * mm});
            skLineSegment(sketch, "E43.9.7.0", {"start": v(36.8, -60.74) * mm, "end": v(34.2, -62.24) * mm});
            skLineSegment(sketch, "E43.1.8.0", {"start": v(79.56, -44.2) * mm, "end": v(78.06, -46.8) * mm});
            skLineSegment(sketch, "E43.3.8.0", {"start": v(79.56, -44.2) * mm, "end": v(62.24, -34.2) * mm});
            skLineSegment(sketch, "E43.6.8.0", {"start": v(78.06, -46.8) * mm, "end": v(60.74, -36.8) * mm});
            skLineSegment(sketch, "E43.9.8.0", {"start": v(62.24, -34.2) * mm, "end": v(60.74, -36.8) * mm});
            skLineSegment(sketch, "E43.1.9.0", {"start": v(91, 1.5) * mm, "end": v(91, -1.5) * mm});
            skLineSegment(sketch, "E43.3.9.0", {"start": v(91, 1.5) * mm, "end": v(71, 1.5) * mm});
            skLineSegment(sketch, "E43.6.9.0", {"start": v(91, -1.5) * mm, "end": v(71, -1.5) * mm});
            skLineSegment(sketch, "E43.9.9.0", {"start": v(71, 1.5) * mm, "end": v(71, -1.5) * mm});
            skLineSegment(sketch, "E43.1.10.0", {"start": v(78.06, 46.8) * mm, "end": v(79.56, 44.2) * mm});
            skLineSegment(sketch, "E43.3.10.0", {"start": v(78.06, 46.8) * mm, "end": v(60.74, 36.8) * mm});
            skLineSegment(sketch, "E43.6.10.0", {"start": v(79.56, 44.2) * mm, "end": v(62.24, 34.2) * mm});
            skLineSegment(sketch, "E43.9.10.0", {"start": v(60.74, 36.8) * mm, "end": v(62.24, 34.2) * mm});
            skLineSegment(sketch, "E43.1.11.0", {"start": v(44.2, 79.56) * mm, "end": v(46.8, 78.06) * mm});
            skLineSegment(sketch, "E43.3.11.0", {"start": v(44.2, 79.56) * mm, "end": v(34.2, 62.24) * mm});
            skLineSegment(sketch, "E43.6.11.0", {"start": v(46.8, 78.06) * mm, "end": v(36.8, 60.74) * mm});
            skLineSegment(sketch, "E43.9.11.0", {"start": v(34.2, 62.24) * mm, "end": v(36.8, 60.74) * mm});
            skSolve(sketch);
        }
        {
            var Q0;
            Q0 = qSketchRegion(id + "F25", true);
            extrude(context, id + "F26", {"entities" : qUnion([Q0]), "operationType" : NewBodyOperationType.REMOVE, "oppositeDirection" : true, "depth" : 0.5 * mm, "offsetDistance" : 25 * mm});
        }
        {
            var Q0;
            Q0=makeQuery(id+"F21.opExtrude","CAP_FACE",FACE,{"disambiguationData":[OSD([sQuery(id+"F20.wireOp",EDGE,"E37"),sQuery(id+"F20.wireOp",EDGE,"E38.0")])],"isStart":false});
            var sketch = newSketch(context, id + "F27", { "sketchPlane" : qUnion([Q0])});
            skLineSegment(sketch, "E44.bottom", {"start": v(-0.75, 90.5) * mm, "end": v(0.75, 90.5) * mm});
            skLineSegment(sketch, "E44.top", {"start": v(-0.75, 78.5) * mm, "end": v(0.75, 78.5) * mm});
            skLineSegment(sketch, "E44.left", {"start": v(-0.75, 90.5) * mm, "end": v(-0.75, 78.5) * mm});
            skLineSegment(sketch, "E44.right", {"start": v(0.75, 90.5) * mm, "end": v(0.75, 78.5) * mm});
            skPoint(sketch, "E44.middle", {"position": v(0, 84.5) * mm});
            skLineSegment(sketch, "E45.1.0", {"start": v(-10.2, 89.93) * mm, "end": v(-8.95, 78) * mm});
            skLineSegment(sketch, "E45.1.1", {"start": v(-10.2, 89.93) * mm, "end": v(-8.71, 90.08) * mm});
            skLineSegment(sketch, "E45.1.2", {"start": v(-8.71, 90.08) * mm, "end": v(-7.46, 78.15) * mm});
            skLineSegment(sketch, "E45.1.3", {"start": v(-8.95, 78) * mm, "end": v(-7.46, 78.15) * mm});
            skLineSegment(sketch, "E45.2.0", {"start": v(-19.55, 88.37) * mm, "end": v(-17.05, 76.63) * mm});
            skLineSegment(sketch, "E45.2.1", {"start": v(-19.55, 88.37) * mm, "end": v(-18.08, 88.68) * mm});
            skLineSegment(sketch, "E45.2.2", {"start": v(-18.08, 88.68) * mm, "end": v(-15.59, 76.94) * mm});
            skLineSegment(sketch, "E45.2.3", {"start": v(-17.05, 76.63) * mm, "end": v(-15.59, 76.94) * mm});
            skLineSegment(sketch, "E45.3.0", {"start": v(-28.68, 85.84) * mm, "end": v(-24.97, 74.43) * mm});
            skLineSegment(sketch, "E45.3.1", {"start": v(-28.68, 85.84) * mm, "end": v(-27.25, 86.3) * mm});
            skLineSegment(sketch, "E45.3.2", {"start": v(-27.25, 86.3) * mm, "end": v(-23.54, 74.89) * mm});
            skLineSegment(sketch, "E45.3.3", {"start": v(-24.97, 74.43) * mm, "end": v(-23.54, 74.89) * mm});
            skLineSegment(sketch, "E45.4.0", {"start": v(-37.5, 82.37) * mm, "end": v(-32.61, 71.4) * mm});
            skLineSegment(sketch, "E45.4.1", {"start": v(-37.5, 82.37) * mm, "end": v(-36.12, 82.98) * mm});
            skLineSegment(sketch, "E45.4.2", {"start": v(-36.12, 82.98) * mm, "end": v(-31.24, 72.02) * mm});
            skLineSegment(sketch, "E45.4.3", {"start": v(-32.61, 71.4) * mm, "end": v(-31.24, 72.02) * mm});
            skLineSegment(sketch, "E45.5.0", {"start": v(-45.9, 78) * mm, "end": v(-39.9, 67.6) * mm});
            skLineSegment(sketch, "E45.5.1", {"start": v(-45.9, 78) * mm, "end": v(-44.6, 78.75) * mm});
            skLineSegment(sketch, "E45.5.2", {"start": v(-44.6, 78.75) * mm, "end": v(-38.6, 68.36) * mm});
            skLineSegment(sketch, "E45.5.3", {"start": v(-39.9, 67.6) * mm, "end": v(-38.6, 68.36) * mm});
            skLineSegment(sketch, "E45.6.0", {"start": v(-53.8, 72.78) * mm, "end": v(-46.75, 63.07) * mm});
            skLineSegment(sketch, "E45.6.1", {"start": v(-53.8, 72.78) * mm, "end": v(-52.59, 73.66) * mm});
            skLineSegment(sketch, "E45.6.2", {"start": v(-52.59, 73.66) * mm, "end": v(-45.53, 63.95) * mm});
            skLineSegment(sketch, "E45.6.3", {"start": v(-46.75, 63.07) * mm, "end": v(-45.53, 63.95) * mm});
            skLineSegment(sketch, "E45.7.0", {"start": v(-61.11, 66.75) * mm, "end": v(-53.08, 57.84) * mm});
            skLineSegment(sketch, "E45.7.1", {"start": v(-61.11, 66.75) * mm, "end": v(-60, 67.76) * mm});
            skLineSegment(sketch, "E45.7.2", {"start": v(-60, 67.76) * mm, "end": v(-51.97, 58.84) * mm});
            skLineSegment(sketch, "E45.7.3", {"start": v(-53.08, 57.84) * mm, "end": v(-51.97, 58.84) * mm});
            skLineSegment(sketch, "E45.8.0", {"start": v(-67.76, 60) * mm, "end": v(-58.84, 51.97) * mm});
            skLineSegment(sketch, "E45.8.1", {"start": v(-67.76, 60) * mm, "end": v(-66.75, 61.11) * mm});
            skLineSegment(sketch, "E45.8.2", {"start": v(-66.75, 61.11) * mm, "end": v(-57.84, 53.08) * mm});
            skLineSegment(sketch, "E45.8.3", {"start": v(-58.84, 51.97) * mm, "end": v(-57.84, 53.08) * mm});
            skLineSegment(sketch, "E45.9.0", {"start": v(-73.66, 52.59) * mm, "end": v(-63.95, 45.53) * mm});
            skLineSegment(sketch, "E45.9.1", {"start": v(-73.66, 52.59) * mm, "end": v(-72.78, 53.8) * mm});
            skLineSegment(sketch, "E45.9.2", {"start": v(-72.78, 53.8) * mm, "end": v(-63.07, 46.75) * mm});
            skLineSegment(sketch, "E45.9.3", {"start": v(-63.95, 45.53) * mm, "end": v(-63.07, 46.75) * mm});
            skLineSegment(sketch, "E45.10.0", {"start": v(-78.75, 44.6) * mm, "end": v(-68.36, 38.6) * mm});
            skLineSegment(sketch, "E45.10.1", {"start": v(-78.75, 44.6) * mm, "end": v(-78, 45.9) * mm});
            skLineSegment(sketch, "E45.10.2", {"start": v(-78, 45.9) * mm, "end": v(-67.6, 39.9) * mm});
            skLineSegment(sketch, "E45.10.3", {"start": v(-68.36, 38.6) * mm, "end": v(-67.6, 39.9) * mm});
            skLineSegment(sketch, "E45.11.0", {"start": v(-82.98, 36.12) * mm, "end": v(-72.02, 31.24) * mm});
            skLineSegment(sketch, "E45.11.1", {"start": v(-82.98, 36.12) * mm, "end": v(-82.37, 37.5) * mm});
            skLineSegment(sketch, "E45.11.2", {"start": v(-82.37, 37.5) * mm, "end": v(-71.4, 32.61) * mm});
            skLineSegment(sketch, "E45.11.3", {"start": v(-72.02, 31.24) * mm, "end": v(-71.4, 32.61) * mm});
            skLineSegment(sketch, "E45.12.0", {"start": v(-86.3, 27.25) * mm, "end": v(-74.89, 23.54) * mm});
            skLineSegment(sketch, "E45.12.1", {"start": v(-86.3, 27.25) * mm, "end": v(-85.84, 28.68) * mm});
            skLineSegment(sketch, "E45.12.2", {"start": v(-85.84, 28.68) * mm, "end": v(-74.43, 24.97) * mm});
            skLineSegment(sketch, "E45.12.3", {"start": v(-74.89, 23.54) * mm, "end": v(-74.43, 24.97) * mm});
            skLineSegment(sketch, "E45.13.0", {"start": v(-88.68, 18.08) * mm, "end": v(-76.94, 15.59) * mm});
            skLineSegment(sketch, "E45.13.1", {"start": v(-88.68, 18.08) * mm, "end": v(-88.37, 19.55) * mm});
            skLineSegment(sketch, "E45.13.2", {"start": v(-88.37, 19.55) * mm, "end": v(-76.63, 17.05) * mm});
            skLineSegment(sketch, "E45.13.3", {"start": v(-76.94, 15.59) * mm, "end": v(-76.63, 17.05) * mm});
            skLineSegment(sketch, "E45.14.0", {"start": v(-90.08, 8.71) * mm, "end": v(-78.15, 7.46) * mm});
            skLineSegment(sketch, "E45.14.1", {"start": v(-90.08, 8.71) * mm, "end": v(-89.93, 10.2) * mm});
            skLineSegment(sketch, "E45.14.2", {"start": v(-89.93, 10.2) * mm, "end": v(-78, 8.95) * mm});
            skLineSegment(sketch, "E45.14.3", {"start": v(-78.15, 7.46) * mm, "end": v(-78, 8.95) * mm});
            skLineSegment(sketch, "E45.15.0", {"start": v(-90.5, -0.75) * mm, "end": v(-78.5, -0.75) * mm});
            skLineSegment(sketch, "E45.15.1", {"start": v(-90.5, -0.75) * mm, "end": v(-90.5, 0.75) * mm});
            skLineSegment(sketch, "E45.15.2", {"start": v(-90.5, 0.75) * mm, "end": v(-78.5, 0.75) * mm});
            skLineSegment(sketch, "E45.15.3", {"start": v(-78.5, -0.75) * mm, "end": v(-78.5, 0.75) * mm});
            skLineSegment(sketch, "E45.16.0", {"start": v(-89.93, -10.2) * mm, "end": v(-78, -8.95) * mm});
            skLineSegment(sketch, "E45.16.1", {"start": v(-89.93, -10.2) * mm, "end": v(-90.08, -8.71) * mm});
            skLineSegment(sketch, "E45.16.2", {"start": v(-90.08, -8.71) * mm, "end": v(-78.15, -7.46) * mm});
            skLineSegment(sketch, "E45.16.3", {"start": v(-78, -8.95) * mm, "end": v(-78.15, -7.46) * mm});
            skLineSegment(sketch, "E45.17.0", {"start": v(-88.37, -19.55) * mm, "end": v(-76.63, -17.05) * mm});
            skLineSegment(sketch, "E45.17.1", {"start": v(-88.37, -19.55) * mm, "end": v(-88.68, -18.08) * mm});
            skLineSegment(sketch, "E45.17.2", {"start": v(-88.68, -18.08) * mm, "end": v(-76.94, -15.59) * mm});
            skLineSegment(sketch, "E45.17.3", {"start": v(-76.63, -17.05) * mm, "end": v(-76.94, -15.59) * mm});
            skLineSegment(sketch, "E45.18.0", {"start": v(-85.84, -28.68) * mm, "end": v(-74.43, -24.97) * mm});
            skLineSegment(sketch, "E45.18.1", {"start": v(-85.84, -28.68) * mm, "end": v(-86.3, -27.25) * mm});
            skLineSegment(sketch, "E45.18.2", {"start": v(-86.3, -27.25) * mm, "end": v(-74.89, -23.54) * mm});
            skLineSegment(sketch, "E45.18.3", {"start": v(-74.43, -24.97) * mm, "end": v(-74.89, -23.54) * mm});
            skLineSegment(sketch, "E45.19.0", {"start": v(-82.37, -37.5) * mm, "end": v(-71.4, -32.61) * mm});
            skLineSegment(sketch, "E45.19.1", {"start": v(-82.37, -37.5) * mm, "end": v(-82.98, -36.12) * mm});
            skLineSegment(sketch, "E45.19.2", {"start": v(-82.98, -36.12) * mm, "end": v(-72.02, -31.24) * mm});
            skLineSegment(sketch, "E45.19.3", {"start": v(-71.4, -32.61) * mm, "end": v(-72.02, -31.24) * mm});
            skLineSegment(sketch, "E45.20.0", {"start": v(-78, -45.9) * mm, "end": v(-67.6, -39.9) * mm});
            skLineSegment(sketch, "E45.20.1", {"start": v(-78, -45.9) * mm, "end": v(-78.75, -44.6) * mm});
            skLineSegment(sketch, "E45.20.2", {"start": v(-78.75, -44.6) * mm, "end": v(-68.36, -38.6) * mm});
            skLineSegment(sketch, "E45.20.3", {"start": v(-67.6, -39.9) * mm, "end": v(-68.36, -38.6) * mm});
            skLineSegment(sketch, "E45.21.0", {"start": v(-72.78, -53.8) * mm, "end": v(-63.07, -46.75) * mm});
            skLineSegment(sketch, "E45.21.1", {"start": v(-72.78, -53.8) * mm, "end": v(-73.66, -52.59) * mm});
            skLineSegment(sketch, "E45.21.2", {"start": v(-73.66, -52.59) * mm, "end": v(-63.95, -45.53) * mm});
            skLineSegment(sketch, "E45.21.3", {"start": v(-63.07, -46.75) * mm, "end": v(-63.95, -45.53) * mm});
            skLineSegment(sketch, "E45.22.0", {"start": v(-66.75, -61.11) * mm, "end": v(-57.84, -53.08) * mm});
            skLineSegment(sketch, "E45.22.1", {"start": v(-66.75, -61.11) * mm, "end": v(-67.76, -60) * mm});
            skLineSegment(sketch, "E45.22.2", {"start": v(-67.76, -60) * mm, "end": v(-58.84, -51.97) * mm});
            skLineSegment(sketch, "E45.22.3", {"start": v(-57.84, -53.08) * mm, "end": v(-58.84, -51.97) * mm});
            skLineSegment(sketch, "E45.23.0", {"start": v(-60, -67.76) * mm, "end": v(-51.97, -58.84) * mm});
            skLineSegment(sketch, "E45.23.1", {"start": v(-60, -67.76) * mm, "end": v(-61.11, -66.75) * mm});
            skLineSegment(sketch, "E45.23.2", {"start": v(-61.11, -66.75) * mm, "end": v(-53.08, -57.84) * mm});
            skLineSegment(sketch, "E45.23.3", {"start": v(-51.97, -58.84) * mm, "end": v(-53.08, -57.84) * mm});
            skLineSegment(sketch, "E45.24.0", {"start": v(-52.59, -73.66) * mm, "end": v(-45.53, -63.95) * mm});
            skLineSegment(sketch, "E45.24.1", {"start": v(-52.59, -73.66) * mm, "end": v(-53.8, -72.78) * mm});
            skLineSegment(sketch, "E45.24.2", {"start": v(-53.8, -72.78) * mm, "end": v(-46.75, -63.07) * mm});
            skLineSegment(sketch, "E45.24.3", {"start": v(-45.53, -63.95) * mm, "end": v(-46.75, -63.07) * mm});
            skLineSegment(sketch, "E45.25.0", {"start": v(-44.6, -78.75) * mm, "end": v(-38.6, -68.36) * mm});
            skLineSegment(sketch, "E45.25.1", {"start": v(-44.6, -78.75) * mm, "end": v(-45.9, -78) * mm});
            skLineSegment(sketch, "E45.25.2", {"start": v(-45.9, -78) * mm, "end": v(-39.9, -67.6) * mm});
            skLineSegment(sketch, "E45.25.3", {"start": v(-38.6, -68.36) * mm, "end": v(-39.9, -67.6) * mm});
            skLineSegment(sketch, "E45.26.0", {"start": v(-36.12, -82.98) * mm, "end": v(-31.24, -72.02) * mm});
            skLineSegment(sketch, "E45.26.1", {"start": v(-36.12, -82.98) * mm, "end": v(-37.5, -82.37) * mm});
            skLineSegment(sketch, "E45.26.2", {"start": v(-37.5, -82.37) * mm, "end": v(-32.61, -71.4) * mm});
            skLineSegment(sketch, "E45.26.3", {"start": v(-31.24, -72.02) * mm, "end": v(-32.61, -71.4) * mm});
            skLineSegment(sketch, "E45.27.0", {"start": v(-27.25, -86.3) * mm, "end": v(-23.54, -74.89) * mm});
            skLineSegment(sketch, "E45.27.1", {"start": v(-27.25, -86.3) * mm, "end": v(-28.68, -85.84) * mm});
            skLineSegment(sketch, "E45.27.2", {"start": v(-28.68, -85.84) * mm, "end": v(-24.97, -74.43) * mm});
            skLineSegment(sketch, "E45.27.3", {"start": v(-23.54, -74.89) * mm, "end": v(-24.97, -74.43) * mm});
            skLineSegment(sketch, "E45.28.0", {"start": v(-18.08, -88.68) * mm, "end": v(-15.59, -76.94) * mm});
            skLineSegment(sketch, "E45.28.1", {"start": v(-18.08, -88.68) * mm, "end": v(-19.55, -88.37) * mm});
            skLineSegment(sketch, "E45.28.2", {"start": v(-19.55, -88.37) * mm, "end": v(-17.05, -76.63) * mm});
            skLineSegment(sketch, "E45.28.3", {"start": v(-15.59, -76.94) * mm, "end": v(-17.05, -76.63) * mm});
            skLineSegment(sketch, "E45.29.0", {"start": v(-8.71, -90.08) * mm, "end": v(-7.46, -78.15) * mm});
            skLineSegment(sketch, "E45.29.1", {"start": v(-8.71, -90.08) * mm, "end": v(-10.2, -89.93) * mm});
            skLineSegment(sketch, "E45.29.2", {"start": v(-10.2, -89.93) * mm, "end": v(-8.95, -78) * mm});
            skLineSegment(sketch, "E45.29.3", {"start": v(-7.46, -78.15) * mm, "end": v(-8.95, -78) * mm});
            skLineSegment(sketch, "E45.30.0", {"start": v(0.75, -90.5) * mm, "end": v(0.75, -78.5) * mm});
            skLineSegment(sketch, "E45.30.1", {"start": v(0.75, -90.5) * mm, "end": v(-0.75, -90.5) * mm});
            skLineSegment(sketch, "E45.30.2", {"start": v(-0.75, -90.5) * mm, "end": v(-0.75, -78.5) * mm});
            skLineSegment(sketch, "E45.30.3", {"start": v(0.75, -78.5) * mm, "end": v(-0.75, -78.5) * mm});
            skLineSegment(sketch, "E45.31.0", {"start": v(10.2, -89.93) * mm, "end": v(8.95, -78) * mm});
            skLineSegment(sketch, "E45.31.1", {"start": v(10.2, -89.93) * mm, "end": v(8.71, -90.08) * mm});
            skLineSegment(sketch, "E45.31.2", {"start": v(8.71, -90.08) * mm, "end": v(7.46, -78.15) * mm});
            skLineSegment(sketch, "E45.31.3", {"start": v(8.95, -78) * mm, "end": v(7.46, -78.15) * mm});
            skLineSegment(sketch, "E45.32.0", {"start": v(19.55, -88.37) * mm, "end": v(17.05, -76.63) * mm});
            skLineSegment(sketch, "E45.32.1", {"start": v(19.55, -88.37) * mm, "end": v(18.08, -88.68) * mm});
            skLineSegment(sketch, "E45.32.2", {"start": v(18.08, -88.68) * mm, "end": v(15.59, -76.94) * mm});
            skLineSegment(sketch, "E45.32.3", {"start": v(17.05, -76.63) * mm, "end": v(15.59, -76.94) * mm});
            skLineSegment(sketch, "E45.33.0", {"start": v(28.68, -85.84) * mm, "end": v(24.97, -74.43) * mm});
            skLineSegment(sketch, "E45.33.1", {"start": v(28.68, -85.84) * mm, "end": v(27.25, -86.3) * mm});
            skLineSegment(sketch, "E45.33.2", {"start": v(27.25, -86.3) * mm, "end": v(23.54, -74.89) * mm});
            skLineSegment(sketch, "E45.33.3", {"start": v(24.97, -74.43) * mm, "end": v(23.54, -74.89) * mm});
            skLineSegment(sketch, "E45.34.0", {"start": v(37.5, -82.37) * mm, "end": v(32.61, -71.4) * mm});
            skLineSegment(sketch, "E45.34.1", {"start": v(37.5, -82.37) * mm, "end": v(36.12, -82.98) * mm});
            skLineSegment(sketch, "E45.34.2", {"start": v(36.12, -82.98) * mm, "end": v(31.24, -72.02) * mm});
            skLineSegment(sketch, "E45.34.3", {"start": v(32.61, -71.4) * mm, "end": v(31.24, -72.02) * mm});
            skLineSegment(sketch, "E45.35.0", {"start": v(45.9, -78) * mm, "end": v(39.9, -67.6) * mm});
            skLineSegment(sketch, "E45.35.1", {"start": v(45.9, -78) * mm, "end": v(44.6, -78.75) * mm});
            skLineSegment(sketch, "E45.35.2", {"start": v(44.6, -78.75) * mm, "end": v(38.6, -68.36) * mm});
            skLineSegment(sketch, "E45.35.3", {"start": v(39.9, -67.6) * mm, "end": v(38.6, -68.36) * mm});
            skLineSegment(sketch, "E45.36.0", {"start": v(53.8, -72.78) * mm, "end": v(46.75, -63.07) * mm});
            skLineSegment(sketch, "E45.36.1", {"start": v(53.8, -72.78) * mm, "end": v(52.59, -73.66) * mm});
            skLineSegment(sketch, "E45.36.2", {"start": v(52.59, -73.66) * mm, "end": v(45.53, -63.95) * mm});
            skLineSegment(sketch, "E45.36.3", {"start": v(46.75, -63.07) * mm, "end": v(45.53, -63.95) * mm});
            skLineSegment(sketch, "E45.37.0", {"start": v(61.11, -66.75) * mm, "end": v(53.08, -57.84) * mm});
            skLineSegment(sketch, "E45.37.1", {"start": v(61.11, -66.75) * mm, "end": v(60, -67.76) * mm});
            skLineSegment(sketch, "E45.37.2", {"start": v(60, -67.76) * mm, "end": v(51.97, -58.84) * mm});
            skLineSegment(sketch, "E45.37.3", {"start": v(53.08, -57.84) * mm, "end": v(51.97, -58.84) * mm});
            skLineSegment(sketch, "E45.38.0", {"start": v(67.76, -60) * mm, "end": v(58.84, -51.97) * mm});
            skLineSegment(sketch, "E45.38.1", {"start": v(67.76, -60) * mm, "end": v(66.75, -61.11) * mm});
            skLineSegment(sketch, "E45.38.2", {"start": v(66.75, -61.11) * mm, "end": v(57.84, -53.08) * mm});
            skLineSegment(sketch, "E45.38.3", {"start": v(58.84, -51.97) * mm, "end": v(57.84, -53.08) * mm});
            skLineSegment(sketch, "E45.39.0", {"start": v(73.66, -52.59) * mm, "end": v(63.95, -45.53) * mm});
            skLineSegment(sketch, "E45.39.1", {"start": v(73.66, -52.59) * mm, "end": v(72.78, -53.8) * mm});
            skLineSegment(sketch, "E45.39.2", {"start": v(72.78, -53.8) * mm, "end": v(63.07, -46.75) * mm});
            skLineSegment(sketch, "E45.39.3", {"start": v(63.95, -45.53) * mm, "end": v(63.07, -46.75) * mm});
            skLineSegment(sketch, "E45.40.0", {"start": v(78.75, -44.6) * mm, "end": v(68.36, -38.6) * mm});
            skLineSegment(sketch, "E45.40.1", {"start": v(78.75, -44.6) * mm, "end": v(78, -45.9) * mm});
            skLineSegment(sketch, "E45.40.2", {"start": v(78, -45.9) * mm, "end": v(67.6, -39.9) * mm});
            skLineSegment(sketch, "E45.40.3", {"start": v(68.36, -38.6) * mm, "end": v(67.6, -39.9) * mm});
            skLineSegment(sketch, "E45.41.0", {"start": v(82.98, -36.12) * mm, "end": v(72.02, -31.24) * mm});
            skLineSegment(sketch, "E45.41.1", {"start": v(82.98, -36.12) * mm, "end": v(82.37, -37.5) * mm});
            skLineSegment(sketch, "E45.41.2", {"start": v(82.37, -37.5) * mm, "end": v(71.4, -32.61) * mm});
            skLineSegment(sketch, "E45.41.3", {"start": v(72.02, -31.24) * mm, "end": v(71.4, -32.61) * mm});
            skLineSegment(sketch, "E45.42.0", {"start": v(86.3, -27.25) * mm, "end": v(74.89, -23.54) * mm});
            skLineSegment(sketch, "E45.42.1", {"start": v(86.3, -27.25) * mm, "end": v(85.84, -28.68) * mm});
            skLineSegment(sketch, "E45.42.2", {"start": v(85.84, -28.68) * mm, "end": v(74.43, -24.97) * mm});
            skLineSegment(sketch, "E45.42.3", {"start": v(74.89, -23.54) * mm, "end": v(74.43, -24.97) * mm});
            skLineSegment(sketch, "E45.43.0", {"start": v(88.68, -18.08) * mm, "end": v(76.94, -15.59) * mm});
            skLineSegment(sketch, "E45.43.1", {"start": v(88.68, -18.08) * mm, "end": v(88.37, -19.55) * mm});
            skLineSegment(sketch, "E45.43.2", {"start": v(88.37, -19.55) * mm, "end": v(76.63, -17.05) * mm});
            skLineSegment(sketch, "E45.43.3", {"start": v(76.94, -15.59) * mm, "end": v(76.63, -17.05) * mm});
            skLineSegment(sketch, "E45.44.0", {"start": v(90.08, -8.71) * mm, "end": v(78.15, -7.46) * mm});
            skLineSegment(sketch, "E45.44.1", {"start": v(90.08, -8.71) * mm, "end": v(89.93, -10.2) * mm});
            skLineSegment(sketch, "E45.44.2", {"start": v(89.93, -10.2) * mm, "end": v(78, -8.95) * mm});
            skLineSegment(sketch, "E45.44.3", {"start": v(78.15, -7.46) * mm, "end": v(78, -8.95) * mm});
            skLineSegment(sketch, "E45.45.0", {"start": v(90.5, 0.75) * mm, "end": v(78.5, 0.75) * mm});
            skLineSegment(sketch, "E45.45.1", {"start": v(90.5, 0.75) * mm, "end": v(90.5, -0.75) * mm});
            skLineSegment(sketch, "E45.45.2", {"start": v(90.5, -0.75) * mm, "end": v(78.5, -0.75) * mm});
            skLineSegment(sketch, "E45.45.3", {"start": v(78.5, 0.75) * mm, "end": v(78.5, -0.75) * mm});
            skLineSegment(sketch, "E45.46.0", {"start": v(89.93, 10.2) * mm, "end": v(78, 8.95) * mm});
            skLineSegment(sketch, "E45.46.1", {"start": v(89.93, 10.2) * mm, "end": v(90.08, 8.71) * mm});
            skLineSegment(sketch, "E45.46.2", {"start": v(90.08, 8.71) * mm, "end": v(78.15, 7.46) * mm});
            skLineSegment(sketch, "E45.46.3", {"start": v(78, 8.95) * mm, "end": v(78.15, 7.46) * mm});
            skLineSegment(sketch, "E45.47.0", {"start": v(88.37, 19.55) * mm, "end": v(76.63, 17.05) * mm});
            skLineSegment(sketch, "E45.47.1", {"start": v(88.37, 19.55) * mm, "end": v(88.68, 18.08) * mm});
            skLineSegment(sketch, "E45.47.2", {"start": v(88.68, 18.08) * mm, "end": v(76.94, 15.59) * mm});
            skLineSegment(sketch, "E45.47.3", {"start": v(76.63, 17.05) * mm, "end": v(76.94, 15.59) * mm});
            skLineSegment(sketch, "E45.48.0", {"start": v(85.84, 28.68) * mm, "end": v(74.43, 24.97) * mm});
            skLineSegment(sketch, "E45.48.1", {"start": v(85.84, 28.68) * mm, "end": v(86.3, 27.25) * mm});
            skLineSegment(sketch, "E45.48.2", {"start": v(86.3, 27.25) * mm, "end": v(74.89, 23.54) * mm});
            skLineSegment(sketch, "E45.48.3", {"start": v(74.43, 24.97) * mm, "end": v(74.89, 23.54) * mm});
            skLineSegment(sketch, "E45.49.0", {"start": v(82.37, 37.5) * mm, "end": v(71.4, 32.61) * mm});
            skLineSegment(sketch, "E45.49.1", {"start": v(82.37, 37.5) * mm, "end": v(82.98, 36.12) * mm});
            skLineSegment(sketch, "E45.49.2", {"start": v(82.98, 36.12) * mm, "end": v(72.02, 31.24) * mm});
            skLineSegment(sketch, "E45.49.3", {"start": v(71.4, 32.61) * mm, "end": v(72.02, 31.24) * mm});
            skLineSegment(sketch, "E45.50.0", {"start": v(78, 45.9) * mm, "end": v(67.6, 39.9) * mm});
            skLineSegment(sketch, "E45.50.1", {"start": v(78, 45.9) * mm, "end": v(78.75, 44.6) * mm});
            skLineSegment(sketch, "E45.50.2", {"start": v(78.75, 44.6) * mm, "end": v(68.36, 38.6) * mm});
            skLineSegment(sketch, "E45.50.3", {"start": v(67.6, 39.9) * mm, "end": v(68.36, 38.6) * mm});
            skLineSegment(sketch, "E45.51.0", {"start": v(72.78, 53.8) * mm, "end": v(63.07, 46.75) * mm});
            skLineSegment(sketch, "E45.51.1", {"start": v(72.78, 53.8) * mm, "end": v(73.66, 52.59) * mm});
            skLineSegment(sketch, "E45.51.2", {"start": v(73.66, 52.59) * mm, "end": v(63.95, 45.53) * mm});
            skLineSegment(sketch, "E45.51.3", {"start": v(63.07, 46.75) * mm, "end": v(63.95, 45.53) * mm});
            skLineSegment(sketch, "E45.52.0", {"start": v(66.75, 61.11) * mm, "end": v(57.84, 53.08) * mm});
            skLineSegment(sketch, "E45.52.1", {"start": v(66.75, 61.11) * mm, "end": v(67.76, 60) * mm});
            skLineSegment(sketch, "E45.52.2", {"start": v(67.76, 60) * mm, "end": v(58.84, 51.97) * mm});
            skLineSegment(sketch, "E45.52.3", {"start": v(57.84, 53.08) * mm, "end": v(58.84, 51.97) * mm});
            skLineSegment(sketch, "E45.53.0", {"start": v(60, 67.76) * mm, "end": v(51.97, 58.84) * mm});
            skLineSegment(sketch, "E45.53.1", {"start": v(60, 67.76) * mm, "end": v(61.11, 66.75) * mm});
            skLineSegment(sketch, "E45.53.2", {"start": v(61.11, 66.75) * mm, "end": v(53.08, 57.84) * mm});
            skLineSegment(sketch, "E45.53.3", {"start": v(51.97, 58.84) * mm, "end": v(53.08, 57.84) * mm});
            skLineSegment(sketch, "E45.54.0", {"start": v(52.59, 73.66) * mm, "end": v(45.53, 63.95) * mm});
            skLineSegment(sketch, "E45.54.1", {"start": v(52.59, 73.66) * mm, "end": v(53.8, 72.78) * mm});
            skLineSegment(sketch, "E45.54.2", {"start": v(53.8, 72.78) * mm, "end": v(46.75, 63.07) * mm});
            skLineSegment(sketch, "E45.54.3", {"start": v(45.53, 63.95) * mm, "end": v(46.75, 63.07) * mm});
            skLineSegment(sketch, "E45.55.0", {"start": v(44.6, 78.75) * mm, "end": v(38.6, 68.36) * mm});
            skLineSegment(sketch, "E45.55.1", {"start": v(44.6, 78.75) * mm, "end": v(45.9, 78) * mm});
            skLineSegment(sketch, "E45.55.2", {"start": v(45.9, 78) * mm, "end": v(39.9, 67.6) * mm});
            skLineSegment(sketch, "E45.55.3", {"start": v(38.6, 68.36) * mm, "end": v(39.9, 67.6) * mm});
            skLineSegment(sketch, "E45.56.0", {"start": v(36.12, 82.98) * mm, "end": v(31.24, 72.02) * mm});
            skLineSegment(sketch, "E45.56.1", {"start": v(36.12, 82.98) * mm, "end": v(37.5, 82.37) * mm});
            skLineSegment(sketch, "E45.56.2", {"start": v(37.5, 82.37) * mm, "end": v(32.61, 71.4) * mm});
            skLineSegment(sketch, "E45.56.3", {"start": v(31.24, 72.02) * mm, "end": v(32.61, 71.4) * mm});
            skLineSegment(sketch, "E45.57.0", {"start": v(27.25, 86.3) * mm, "end": v(23.54, 74.89) * mm});
            skLineSegment(sketch, "E45.57.1", {"start": v(27.25, 86.3) * mm, "end": v(28.68, 85.84) * mm});
            skLineSegment(sketch, "E45.57.2", {"start": v(28.68, 85.84) * mm, "end": v(24.97, 74.43) * mm});
            skLineSegment(sketch, "E45.57.3", {"start": v(23.54, 74.89) * mm, "end": v(24.97, 74.43) * mm});
            skLineSegment(sketch, "E45.58.0", {"start": v(18.08, 88.68) * mm, "end": v(15.59, 76.94) * mm});
            skLineSegment(sketch, "E45.58.1", {"start": v(18.08, 88.68) * mm, "end": v(19.55, 88.37) * mm});
            skLineSegment(sketch, "E45.58.2", {"start": v(19.55, 88.37) * mm, "end": v(17.05, 76.63) * mm});
            skLineSegment(sketch, "E45.58.3", {"start": v(15.59, 76.94) * mm, "end": v(17.05, 76.63) * mm});
            skLineSegment(sketch, "E45.59.0", {"start": v(8.71, 90.08) * mm, "end": v(7.46, 78.15) * mm});
            skLineSegment(sketch, "E45.59.1", {"start": v(8.71, 90.08) * mm, "end": v(10.2, 89.93) * mm});
            skLineSegment(sketch, "E45.59.2", {"start": v(10.2, 89.93) * mm, "end": v(8.95, 78) * mm});
            skLineSegment(sketch, "E45.59.3", {"start": v(7.46, 78.15) * mm, "end": v(8.95, 78) * mm});
            skPoint(sketch, "E45.center", {"position": v(0, 0) * mm});
            skSolve(sketch);
        }
        {
            var Q0;
            Q0 = qSketchRegion(id + "F27", true);
            extrude(context, id + "F28", {"entities" : qUnion([Q0]), "operationType" : NewBodyOperationType.REMOVE, "oppositeDirection" : true, "depth" : 0.2 * mm, "offsetDistance" : 25 * mm});
        }
        {
            var Q0;
            Q0=makeQuery(id+"F26.boolean.opBoolean","COPY",FACE,{"derivedFrom":makeQuery(id+"F26.opExtrude","CAP_FACE",FACE,{"disambiguationData":[OSD([sQuery(id+"F25.wireOp",EDGE,"E41.bottom"),sQuery(id+"F25.wireOp",EDGE,"E41.top"),sQuery(id+"F25.wireOp",EDGE,"E41.left"),sQuery(id+"F25.wireOp",EDGE,"E41.right")])],"isStart":false})});
            extrude(context, id + "F29", {"entities" : qUnion([Q0]), "depth" : 1 * mm, "offsetDistance" : 25 * mm});
        }
        {
            var Q0;
            Q0=makeQuery(id+"F28.boolean.opBoolean","COPY",FACE,{"derivedFrom":makeQuery(id+"F28.opExtrude","CAP_FACE",FACE,{"disambiguationData":[OSD([sQuery(id+"F27.wireOp",EDGE,"E45.59.0"),sQuery(id+"F27.wireOp",EDGE,"E45.59.1"),sQuery(id+"F27.wireOp",EDGE,"E45.59.2"),sQuery(id+"F27.wireOp",EDGE,"E45.59.3")])],"isStart":false})});
            extrude(context, id + "F30", {"entities" : qUnion([Q0]), "depth" : 0.4 * mm, "offsetDistance" : 25 * mm});
        }
        {
            var Q0;
            Q0=makeQuery(id+"F15.opExtrude","CAP_FACE",FACE,{"disambiguationData":[OSD([sQuery(id+"F14.wireOp",EDGE,"E21.0"),sQuery(id+"F14.wireOp",EDGE,"E22"),sQuery(id+"F14.wireOp",EDGE,"E23"),sQuery(id+"F14.wireOp",EDGE,"E24"),sQuery(id+"F14.wireOp",EDGE,"E25.MirrorCS"),sQuery(id+"F14.wireOp",EDGE,"E26.MirrorCS"),sQuery(id+"F14.wireOp",EDGE,"E27.1.0"),sQuery(id+"F14.wireOp",EDGE,"E27.1.1"),sQuery(id+"F14.wireOp",EDGE,"E27.1.2"),sQuery(id+"F14.wireOp",EDGE,"E27.1.3"),sQuery(id+"F14.wireOp",EDGE,"E27.2.0"),sQuery(id+"F14.wireOp",EDGE,"E27.2.1"),sQuery(id+"F14.wireOp",EDGE,"E27.2.2"),sQuery(id+"F14.wireOp",EDGE,"E27.2.3"),sQuery(id+"F14.wireOp",EDGE,"E28.2.3.0"),sQuery(id+"F14.wireOp",EDGE,"E28.3.3.0"),sQuery(id+"F14.wireOp",EDGE,"E28.6.3.0"),sQuery(id+"F14.wireOp",EDGE,"E28.9.3.0"),sQuery(id+"F14.wireOp",EDGE,"E28.2.4.0"),sQuery(id+"F14.wireOp",EDGE,"E28.3.4.0"),sQuery(id+"F14.wireOp",EDGE,"E28.6.4.0"),sQuery(id+"F14.wireOp",EDGE,"E28.9.4.0"),sQuery(id+"F14.wireOp",EDGE,"E28.2.5.0"),sQuery(id+"F14.wireOp",EDGE,"E28.3.5.0"),sQuery(id+"F14.wireOp",EDGE,"E28.6.5.0"),sQuery(id+"F14.wireOp",EDGE,"E28.9.5.0"),sQuery(id+"F14.wireOp",EDGE,"E28.2.6.0"),sQuery(id+"F14.wireOp",EDGE,"E28.3.6.0"),sQuery(id+"F14.wireOp",EDGE,"E28.6.6.0"),sQuery(id+"F14.wireOp",EDGE,"E28.9.6.0"),sQuery(id+"F14.wireOp",EDGE,"E28.2.7.0"),sQuery(id+"F14.wireOp",EDGE,"E28.3.7.0"),sQuery(id+"F14.wireOp",EDGE,"E28.6.7.0"),sQuery(id+"F14.wireOp",EDGE,"E28.9.7.0"),sQuery(id+"F14.wireOp",EDGE,"E28.2.8.0"),sQuery(id+"F14.wireOp",EDGE,"E28.3.8.0"),sQuery(id+"F14.wireOp",EDGE,"E28.6.8.0"),sQuery(id+"F14.wireOp",EDGE,"E28.9.8.0"),sQuery(id+"F14.wireOp",EDGE,"E28.2.9.0"),sQuery(id+"F14.wireOp",EDGE,"E28.3.9.0"),sQuery(id+"F14.wireOp",EDGE,"E28.6.9.0"),sQuery(id+"F14.wireOp",EDGE,"E28.9.9.0"),sQuery(id+"F14.wireOp",EDGE,"E28.2.10.0"),sQuery(id+"F14.wireOp",EDGE,"E28.3.10.0"),sQuery(id+"F14.wireOp",EDGE,"E28.6.10.0"),sQuery(id+"F14.wireOp",EDGE,"E28.9.10.0"),sQuery(id+"F14.wireOp",EDGE,"E28.2.11.0"),sQuery(id+"F14.wireOp",EDGE,"E28.3.11.0"),sQuery(id+"F14.wireOp",EDGE,"E28.6.11.0"),sQuery(id+"F14.wireOp",EDGE,"E28.9.11.0"),sQuery(id+"F14.wireOp",EDGE,"E28.2.12.0"),sQuery(id+"F14.wireOp",EDGE,"E28.3.12.0"),sQuery(id+"F14.wireOp",EDGE,"E28.6.12.0"),sQuery(id+"F14.wireOp",EDGE,"E28.9.12.0"),sQuery(id+"F14.wireOp",EDGE,"E28.2.13.0"),sQuery(id+"F14.wireOp",EDGE,"E28.3.13.0"),sQuery(id+"F14.wireOp",EDGE,"E28.6.13.0"),sQuery(id+"F14.wireOp",EDGE,"E28.9.13.0"),sQuery(id+"F14.wireOp",EDGE,"E28.2.14.0"),sQuery(id+"F14.wireOp",EDGE,"E28.3.14.0"),sQuery(id+"F14.wireOp",EDGE,"E28.6.14.0"),sQuery(id+"F14.wireOp",EDGE,"E28.9.14.0"),sQuery(id+"F14.wireOp",EDGE,"E28.2.15.0"),sQuery(id+"F14.wireOp",EDGE,"E28.3.15.0"),sQuery(id+"F14.wireOp",EDGE,"E28.6.15.0"),sQuery(id+"F14.wireOp",EDGE,"E28.9.15.0"),sQuery(id+"F14.wireOp",EDGE,"E28.2.16.0"),sQuery(id+"F14.wireOp",EDGE,"E28.3.16.0"),sQuery(id+"F14.wireOp",EDGE,"E28.6.16.0"),sQuery(id+"F14.wireOp",EDGE,"E28.9.16.0"),sQuery(id+"F14.wireOp",EDGE,"E28.2.17.0"),sQuery(id+"F14.wireOp",EDGE,"E28.3.17.0"),sQuery(id+"F14.wireOp",EDGE,"E28.6.17.0"),sQuery(id+"F14.wireOp",EDGE,"E28.9.17.0"),sQuery(id+"F14.wireOp",EDGE,"E28.2.18.0"),sQuery(id+"F14.wireOp",EDGE,"E28.3.18.0"),sQuery(id+"F14.wireOp",EDGE,"E28.6.18.0"),sQuery(id+"F14.wireOp",EDGE,"E28.9.18.0"),sQuery(id+"F14.wireOp",EDGE,"E28.2.19.0"),sQuery(id+"F14.wireOp",EDGE,"E28.3.19.0"),sQuery(id+"F14.wireOp",EDGE,"E28.6.19.0"),sQuery(id+"F14.wireOp",EDGE,"E28.9.19.0"),sQuery(id+"F14.wireOp",EDGE,"E28.2.20.0"),sQuery(id+"F14.wireOp",EDGE,"E28.3.20.0"),sQuery(id+"F14.wireOp",EDGE,"E28.6.20.0"),sQuery(id+"F14.wireOp",EDGE,"E28.9.20.0"),sQuery(id+"F14.wireOp",EDGE,"E28.2.21.0"),sQuery(id+"F14.wireOp",EDGE,"E28.3.21.0"),sQuery(id+"F14.wireOp",EDGE,"E28.6.21.0"),sQuery(id+"F14.wireOp",EDGE,"E28.9.21.0"),sQuery(id+"F14.wireOp",EDGE,"E28.2.22.0"),sQuery(id+"F14.wireOp",EDGE,"E28.3.22.0"),sQuery(id+"F14.wireOp",EDGE,"E28.6.22.0"),sQuery(id+"F14.wireOp",EDGE,"E28.9.22.0"),sQuery(id+"F14.wireOp",EDGE,"E28.2.23.0"),sQuery(id+"F14.wireOp",EDGE,"E28.3.23.0"),sQuery(id+"F14.wireOp",EDGE,"E28.6.23.0"),sQuery(id+"F14.wireOp",EDGE,"E28.9.23.0"),sQuery(id+"F14.wireOp",EDGE,"E28.2.24.0"),sQuery(id+"F14.wireOp",EDGE,"E28.3.24.0"),sQuery(id+"F14.wireOp",EDGE,"E28.6.24.0"),sQuery(id+"F14.wireOp",EDGE,"E28.9.24.0"),sQuery(id+"F14.wireOp",EDGE,"E28.2.25.0"),sQuery(id+"F14.wireOp",EDGE,"E28.3.25.0"),sQuery(id+"F14.wireOp",EDGE,"E28.6.25.0"),sQuery(id+"F14.wireOp",EDGE,"E28.9.25.0"),sQuery(id+"F14.wireOp",EDGE,"E28.2.26.0"),sQuery(id+"F14.wireOp",EDGE,"E28.3.26.0"),sQuery(id+"F14.wireOp",EDGE,"E28.6.26.0"),sQuery(id+"F14.wireOp",EDGE,"E28.9.26.0"),sQuery(id+"F14.wireOp",EDGE,"E28.2.27.0"),sQuery(id+"F14.wireOp",EDGE,"E28.3.27.0"),sQuery(id+"F14.wireOp",EDGE,"E28.6.27.0"),sQuery(id+"F14.wireOp",EDGE,"E28.9.27.0"),sQuery(id+"F14.wireOp",EDGE,"E28.2.28.0"),sQuery(id+"F14.wireOp",EDGE,"E28.3.28.0"),sQuery(id+"F14.wireOp",EDGE,"E28.6.28.0"),sQuery(id+"F14.wireOp",EDGE,"E28.9.28.0"),sQuery(id+"F14.wireOp",EDGE,"E28.2.29.0"),sQuery(id+"F14.wireOp",EDGE,"E28.3.29.0"),sQuery(id+"F14.wireOp",EDGE,"E28.6.29.0"),sQuery(id+"F14.wireOp",EDGE,"E28.9.29.0"),sQuery(id+"F14.wireOp",EDGE,"E28.2.30.0"),sQuery(id+"F14.wireOp",EDGE,"E28.3.30.0"),sQuery(id+"F14.wireOp",EDGE,"E28.6.30.0"),sQuery(id+"F14.wireOp",EDGE,"E28.9.30.0"),sQuery(id+"F14.wireOp",EDGE,"E28.2.31.0"),sQuery(id+"F14.wireOp",EDGE,"E28.3.31.0"),sQuery(id+"F14.wireOp",EDGE,"E28.6.31.0"),sQuery(id+"F14.wireOp",EDGE,"E28.9.31.0"),sQuery(id+"F14.wireOp",EDGE,"E28.2.32.0"),sQuery(id+"F14.wireOp",EDGE,"E28.3.32.0"),sQuery(id+"F14.wireOp",EDGE,"E28.6.32.0"),sQuery(id+"F14.wireOp",EDGE,"E28.9.32.0"),sQuery(id+"F14.wireOp",EDGE,"E28.2.33.0"),sQuery(id+"F14.wireOp",EDGE,"E28.3.33.0"),sQuery(id+"F14.wireOp",EDGE,"E28.6.33.0"),sQuery(id+"F14.wireOp",EDGE,"E28.9.33.0"),sQuery(id+"F14.wireOp",EDGE,"E28.2.34.0"),sQuery(id+"F14.wireOp",EDGE,"E28.3.34.0"),sQuery(id+"F14.wireOp",EDGE,"E28.6.34.0"),sQuery(id+"F14.wireOp",EDGE,"E28.9.34.0"),sQuery(id+"F14.wireOp",EDGE,"E28.2.35.0"),sQuery(id+"F14.wireOp",EDGE,"E28.3.35.0"),sQuery(id+"F14.wireOp",EDGE,"E28.6.35.0"),sQuery(id+"F14.wireOp",EDGE,"E28.9.35.0"),sQuery(id+"F14.wireOp",EDGE,"E28.2.36.0"),sQuery(id+"F14.wireOp",EDGE,"E28.3.36.0"),sQuery(id+"F14.wireOp",EDGE,"E28.6.36.0"),sQuery(id+"F14.wireOp",EDGE,"E28.9.36.0"),sQuery(id+"F14.wireOp",EDGE,"E28.2.37.0"),sQuery(id+"F14.wireOp",EDGE,"E28.3.37.0"),sQuery(id+"F14.wireOp",EDGE,"E28.6.37.0"),sQuery(id+"F14.wireOp",EDGE,"E28.9.37.0"),sQuery(id+"F14.wireOp",EDGE,"E28.2.38.0"),sQuery(id+"F14.wireOp",EDGE,"E28.3.38.0"),sQuery(id+"F14.wireOp",EDGE,"E28.6.38.0"),sQuery(id+"F14.wireOp",EDGE,"E28.9.38.0"),sQuery(id+"F14.wireOp",EDGE,"E28.2.39.0"),sQuery(id+"F14.wireOp",EDGE,"E28.3.39.0"),sQuery(id+"F14.wireOp",EDGE,"E28.6.39.0"),sQuery(id+"F14.wireOp",EDGE,"E28.9.39.0")])],"isStart":false});
            var sketch = newSketch(context, id + "F31", { "sketchPlane" : qUnion([Q0])});
            skCircle(sketch, "E46.0", {"center": v(0, 0) * mm, "radius": 3 * mm});
            skCircle(sketch, "E47.0", {"center": v(0, 0) * mm, "radius": 5 * mm});
            skSolve(sketch);
        }
        {
            var Q0;
            Q0 = qSketchRegion(id + "F31", true);
            extrude(context, id + "F32", {"entities" : qUnion([Q0]), "operationType" : NewBodyOperationType.ADD, "depth" : 5 * mm, "offsetDistance" : 25 * mm});
        }
        {
            var Q0;
            Q0=makeQuery(id+"F32.opExtrude","CAP_FACE",FACE,{"disambiguationData":[OSD([sQuery(id+"F31.wireOp",EDGE,"E46.0"),sQuery(id+"F31.wireOp",EDGE,"E47.0")])],"isStart":false});
            var sketch = newSketch(context, id + "F33", { "sketchPlane" : qUnion([Q0])});
            skCircle(sketch, "E48.0", {"center": v(0, 0) * mm, "radius": 5 * mm});
            skCircle(sketch, "E49.0", {"center": v(0, 0) * mm, "radius": 3 * mm});
            skLineSegment(sketch, "E50", {"start": v(0, 50) * mm, "end": v(1.5, 50) * mm});
            skLineSegment(sketch, "E51", {"start": v(1.5, 50) * mm, "end": v(3, 4) * mm});
            skLineSegment(sketch, "E52.MirrorCS", {"start": v(0, 50) * mm, "end": v(-1.5, 50) * mm});
            skLineSegment(sketch, "E53.MirrorCS", {"start": v(-1.5, 50) * mm, "end": v(-3, 4) * mm});
            skSolve(sketch);
        }
        {
            var Q0;
            Q0 = qSketchRegion(id + "F33", true);
            extrude(context, id + "F34", {"entities" : qUnion([Q0]), "operationType" : NewBodyOperationType.ADD, "depth" : 1 * mm, "offsetDistance" : 25 * mm});
        }
        {
            var Q0;
            Q0=makeQuery(id+"F6.opExtrude","CAP_FACE",FACE,{"disambiguationData":[OSD([sQuery(id+"F0.wireOp",EDGE,"E0")])],"isStart":false});
            var sketch = newSketch(context, id + "F35", { "sketchPlane" : qUnion([Q0])});
            skCircle(sketch, "E54", {"center": v(0, 0) * mm, "radius": 5 * mm});
            skLineSegment(sketch, "E55", {"start": v(0, 80) * mm, "end": v(0.5, 80) * mm});
            skLineSegment(sketch, "E56", {"start": v(0.5, 80) * mm, "end": v(2, 4.58) * mm});
            skLineSegment(sketch, "E57.MirrorCS", {"start": v(0, 80) * mm, "end": v(-0.5, 80) * mm});
            skLineSegment(sketch, "E58.MirrorCS", {"start": v(-0.5, 80) * mm, "end": v(-2, 4.58) * mm});
            skSolve(sketch);
        }
        {
            var Q0;
            Q0 = qSketchRegion(id + "F35", true);
            extrude(context, id + "F36", {"entities" : qUnion([Q0]), "operationType" : NewBodyOperationType.ADD, "oppositeDirection" : true, "depth" : 1 * mm, "offsetDistance" : 25 * mm});
        }
    });
